annotation { "Feature Type Name" : "Feature", "Feature Type Description" : "" }
export const myFeature = defineFeature(function(context is Context, id is Id, definition is map)
    precondition{}
    {
        {
            var Q0;
            Q0=qCreatedBy(makeId("Top.planeOp"),FACE);
            var sketch = newSketch(context, id + "F0", { "sketchPlane" : qUnion([Q0])});
            skLineSegment(sketch, "E0.bottom", {"start": v(75, -105) * mm, "end": v(-75, -105) * mm});
            skLineSegment(sketch, "E0.top", {"start": v(75, 105) * mm, "end": v(-75, 105) * mm});
            skLineSegment(sketch, "E0.left", {"start": v(75, -105) * mm, "end": v(75, 105) * mm});
            skLineSegment(sketch, "E0.right", {"start": v(-75, -105) * mm, "end": v(-75, 105) * mm});
            skPoint(sketch, "E0.middle", {"position": v(0, 0) * mm});
            skLineSegment(sketch, "E1.bottom", {"start": v(77, -107) * mm, "end": v(-77, -107) * mm});
            skLineSegment(sketch, "E1.top", {"start": v(77, 107) * mm, "end": v(-77, 107) * mm});
            skLineSegment(sketch, "E1.left", {"start": v(77, -107) * mm, "end": v(77, 107) * mm});
            skLineSegment(sketch, "E1.right", {"start": v(-77, -107) * mm, "end": v(-77, 107) * mm});
            skSolve(sketch);
        }
        {
            var Q0;
            Q0=makeQuery(id+"F0.imprint","IMPRINT",FACE,{"disambiguationData":[TD([[makeQuery(id+"F0.imprint","IMPRINT",EDGE,{"derivedFrom":sQuery(id+"F0.wireOp",EDGE,"E0.bottom")}),-1.0]])]});
            extrude(context, id + "F1", {"entities" : qUnion([Q0]), "depth" : 8 * mm, "offsetDistance" : 25 * mm});
        }
        {
            var Q0;
            Q0=makeQuery(id+"F0.imprint","IMPRINT",FACE,{"disambiguationData":[TD([[makeQuery(id+"F0.imprint","IMPRINT",EDGE,{"derivedFrom":sQuery(id+"F0.wireOp",EDGE,"E0.bottom")}),1.0]])]});
            extrude(context, id + "F2", {"entities" : qUnion([Q0]), "operationType" : NewBodyOperationType.ADD, "depth" : 100 * mm, "offsetDistance" : 25 * mm});
        }
        {
            var Q0;
            Q0=makeQuery(id+"F2.opExtrude","SWEPT_FACE",FACE,{"disambiguationData":[OSD([sQuery(id+"F0.wireOp",EDGE,"E0.right")])]});
            var sketch = newSketch(context, id + "F3", { "sketchPlane" : qUnion([Q0])});
            skLineSegment(sketch, "E2.bottom", {"start": v(-6.25, 88.1) * mm, "end": v(14.25, 88.1) * mm});
            skLineSegment(sketch, "E2.top", {"start": v(-6.25, 76.6) * mm, "end": v(14.25, 76.6) * mm});
            skLineSegment(sketch, "E2.left", {"start": v(-6.25, 88.1) * mm, "end": v(-6.25, 76.6) * mm});
            skLineSegment(sketch, "E2.right", {"start": v(14.25, 88.1) * mm, "end": v(14.25, 76.6) * mm});
            skLineSegment(sketch, "E3.bottom", {"start": v(-7, 38.82) * mm, "end": v(15, 38.82) * mm});
            skLineSegment(sketch, "E3.top", {"start": v(-7, 15.82) * mm, "end": v(15, 15.82) * mm});
            skLineSegment(sketch, "E3.left", {"start": v(-7, 38.82) * mm, "end": v(-7, 15.82) * mm});
            skLineSegment(sketch, "E3.right", {"start": v(15, 38.82) * mm, "end": v(15, 15.82) * mm});
            skLineSegment(sketch, "E4.bottom", {"start": v(39.95, 34) * mm, "end": v(59.95, 34) * mm});
            skLineSegment(sketch, "E4.top", {"start": v(39.95, 26) * mm, "end": v(59.95, 26) * mm});
            skLineSegment(sketch, "E4.left", {"start": v(59.95, 34) * mm, "end": v(59.95, 26) * mm});
            skLineSegment(sketch, "E4.right", {"start": v(39.95, 34) * mm, "end": v(39.95, 26) * mm});
            skPoint(sketch, "E5", {"position": v(49.95, 34) * mm});
            skLineSegment(sketch, "E6.0.1.0", {"start": v(59.95, 61) * mm, "end": v(59.95, 53) * mm});
            skLineSegment(sketch, "E6.0.1.1", {"start": v(39.95, 53) * mm, "end": v(59.95, 53) * mm});
            skLineSegment(sketch, "E6.0.1.2", {"start": v(39.95, 61) * mm, "end": v(39.95, 53) * mm});
            skLineSegment(sketch, "E6.0.1.3", {"start": v(39.95, 61) * mm, "end": v(59.95, 61) * mm});
            skPoint(sketch, "E6.0.1.4", {"position": v(49.95, 61) * mm});
            skLineSegment(sketch, "E6.0.2.0", {"start": v(59.95, 88) * mm, "end": v(59.95, 80) * mm});
            skLineSegment(sketch, "E6.0.2.1", {"start": v(39.95, 80) * mm, "end": v(59.95, 80) * mm});
            skLineSegment(sketch, "E6.0.2.2", {"start": v(39.95, 88) * mm, "end": v(39.95, 80) * mm});
            skLineSegment(sketch, "E6.0.2.3", {"start": v(39.95, 88) * mm, "end": v(59.95, 88) * mm});
            skPoint(sketch, "E6.0.2.4", {"position": v(49.95, 88) * mm});
            skLineSegment(sketch, "E6.direction1", {"start": v(39.95, 26) * mm, "end": v(62.2, 26) * mm, "construction": true});
            skLineSegment(sketch, "E6.direction2", {"start": v(39.95, 26) * mm, "end": v(39.95, 53) * mm, "construction": true});
            skLineSegment(sketch, "E7.bottom", {"start": v(-6.25, 63.2) * mm, "end": v(14.25, 63.2) * mm});
            skLineSegment(sketch, "E7.top", {"start": v(-6.25, 53.7) * mm, "end": v(14.25, 53.7) * mm});
            skLineSegment(sketch, "E7.left", {"start": v(-6.25, 63.2) * mm, "end": v(-6.25, 53.7) * mm});
            skLineSegment(sketch, "E7.right", {"start": v(14.25, 63.2) * mm, "end": v(14.25, 53.7) * mm});
            skCircle(sketch, "E8", {"center": v(-55, 68) * mm, "radius": 4.5 * mm});
            skPoint(sketch, "E9", {"position": v(-79.5, 38) * mm});
            skPoint(sketch, "E10", {"position": v(77.48, 100) * mm});
            skPoint(sketch, "E11", {"position": v(77.48, 0) * mm});
            skPoint(sketch, "E12", {"position": v(105, 100) * mm});
            skPoint(sketch, "E13", {"position": v(-105, 100) * mm});
            skCircle(sketch, "E14", {"center": v(-79.5, 38) * mm, "radius": 3.5 * mm});
            skPoint(sketch, "E15", {"position": v(4, 15.82) * mm});
            skPoint(sketch, "E16", {"position": v(4, 63.2) * mm});
            skPoint(sketch, "E17", {"position": v(4, 76.6) * mm});
            skSolve(sketch);
        }
        {
            var Q0;
            Q0=makeQuery(id+"F3.imprint","IMPRINT",FACE,{"disambiguationData":[TD([[makeQuery(id+"F3.imprint","IMPRINT",EDGE,{"derivedFrom":sQuery(id+"F3.wireOp",EDGE,"E2.bottom")}),-1.0]])]});
            var Q1;
            Q1=makeQuery(id+"F3.imprint","IMPRINT",FACE,{"disambiguationData":[TD([[makeQuery(id+"F3.imprint","IMPRINT",EDGE,{"derivedFrom":sQuery(id+"F3.wireOp",EDGE,"E3.bottom")}),-1.0]])]});
            var Q2;
            Q2=makeQuery(id+"F3.imprint","IMPRINT",FACE,{"disambiguationData":[TD([[makeQuery(id+"F3.imprint","IMPRINT",EDGE,{"derivedFrom":sQuery(id+"F3.wireOp",EDGE,"E4.bottom")}),-1.0]])]});
            var Q3;
            Q3=makeQuery(id+"F3.imprint","IMPRINT",FACE,{"disambiguationData":[TD([[makeQuery(id+"F3.imprint","IMPRINT",EDGE,{"derivedFrom":sQuery(id+"F3.wireOp",EDGE,"E6.0.1.0")}),-1.0]])]});
            var Q4;
            Q4=makeQuery(id+"F3.imprint","IMPRINT",FACE,{"disambiguationData":[TD([[makeQuery(id+"F3.imprint","IMPRINT",EDGE,{"derivedFrom":sQuery(id+"F3.wireOp",EDGE,"E6.0.2.0")}),-1.0]])]});
            var Q5;
            Q5=makeQuery(id+"F3.imprint","IMPRINT",FACE,{"disambiguationData":[TD([[makeQuery(id+"F3.imprint","IMPRINT",EDGE,{"derivedFrom":sQuery(id+"F3.wireOp",EDGE,"E7.bottom")}),-1.0]])]});
            var Q6;
            Q6=makeQuery(id+"F3.imprint","IMPRINT",FACE,{"disambiguationData":[TD([[makeQuery(id+"F3.imprint","IMPRINT",EDGE,{"derivedFrom":sQuery(id+"F3.wireOp",EDGE,"E8")}),1.0]])]});
            extrude(context, id + "F4", {"entities" : qUnion([Q0, Q1, Q2, Q3, Q4, Q5, Q6]), "operationType" : NewBodyOperationType.REMOVE, "endBound" : BoundingType.UP_TO_NEXT, "oppositeDirection" : true, "depth" : 25 * mm, "offsetDistance" : 25 * mm});
        }
        {
            var Q0;
            Q0=makeQuery(id+"F2.opExtrude","SWEPT_FACE",FACE,{"disambiguationData":[OSD([sQuery(id+"F0.wireOp",EDGE,"E1.right")])]});
            var sketch = newSketch(context, id + "F5", { "sketchPlane" : qUnion([Q0])});
            skPoint(sketch, "E18", {"position": v(-16, 82.35) * mm});
            skPoint(sketch, "E18.positionSnap0", {"position": v(-14.25, 82.35) * mm});
            skPoint(sketch, "E19.positionSnap0", {"position": v(6.25, 82.35) * mm});
            skPoint(sketch, "E20", {"position": v(9.75, 27.32) * mm});
            skPoint(sketch, "E20.positionSnap0", {"position": v(7, 27.32) * mm});
            skPoint(sketch, "E21", {"position": v(-17.75, 27.32) * mm});
            skPoint(sketch, "E21.positionSnap0", {"position": v(-15, 27.32) * mm});
            skPoint(sketch, "E22", {"position": v(55, 68) * mm});
            skPoint(sketch, "E23", {"position": v(62.5, 68) * mm});
            skPoint(sketch, "E24", {"position": v(47.5, 68) * mm});
            skPoint(sketch, "E25", {"position": v(8, 82.35) * mm});
            skPoint(sketch, "E26", {"position": v(9.75, 58.44) * mm});
            skPoint(sketch, "E26.positionSnap0", {"position": v(6.25, 58.44) * mm});
            skPoint(sketch, "E27", {"position": v(-17.75, 58.44) * mm});
            skPoint(sketch, "E27.positionSnap0", {"position": v(-14.25, 58.44) * mm});
            skSolve(sketch);
        }
        {
            var Q0;
            Q0=sQuery(id+"F5.wireOp",VERTEX,"E18");
            var Q1;
            Q1=sQuery(id+"F5.wireOp",VERTEX,"E19");
            var Q2;
            Q2=sQuery(id+"F5.wireOp",VERTEX,"E25");
            var Q3;
            Q3=sQuery(id+"F5.wireOp",VERTEX,"E27");
            var Q4;
            Q4=sQuery(id+"F5.wireOp",VERTEX,"E26");
            var Q5;
            Q5=makeQuery(id+"F1.opExtrude","SWEPT_BODY",BODY,{"disambiguationData":[OSD([sQuery(id+"F0.wireOp",EDGE,"E0.bottom"),sQuery(id+"F0.wireOp",EDGE,"E0.top"),sQuery(id+"F0.wireOp",EDGE,"E0.left"),sQuery(id+"F0.wireOp",EDGE,"E0.right")])]});
            hole(context, id + "F6", {"style" : HoleStyle.SIMPLE, "endStyle" : HoleEndStyle.BLIND, "holeDiameter" : 2.2 * mm, "majorDiameter" : 5 * mm, "holeDepth" : 5 * mm, "isTappedThrough" : true, "tappedDepth" : 12 * mm, "tapClearance" : 3, "locations" : qUnion([Q0, Q1, Q2, Q3, Q4]), "scope" : qUnion([Q5])});
        }
        {
            var Q0;
            Q0=sQuery(id+"F5.wireOp",VERTEX,"E20");
            var Q1;
            Q1=sQuery(id+"F5.wireOp",VERTEX,"E21");
            var Q2;
            Q2=makeQuery(id+"F1.opExtrude","SWEPT_BODY",BODY,{"disambiguationData":[OSD([sQuery(id+"F0.wireOp",EDGE,"E0.bottom"),sQuery(id+"F0.wireOp",EDGE,"E0.top"),sQuery(id+"F0.wireOp",EDGE,"E0.left"),sQuery(id+"F0.wireOp",EDGE,"E0.right")])]});
            hole(context, id + "F7", {"style" : HoleStyle.SIMPLE, "endStyle" : HoleEndStyle.BLIND, "holeDiameter" : 3.3 * mm, "majorDiameter" : 5 * mm, "holeDepth" : 5 * mm, "isTappedThrough" : true, "tappedDepth" : 12 * mm, "tapClearance" : 3, "locations" : qUnion([Q0, Q1]), "scope" : qUnion([Q2])});
        }
        {
            var Q0;
            Q0=makeQuery(id+"F2.opExtrude","SWEPT_FACE",FACE,{"disambiguationData":[OSD([sQuery(id+"F0.wireOp",EDGE,"E1.right")])]});
            var sketch = newSketch(context, id + "F8", { "sketchPlane" : qUnion([Q0])});
            skText(sketch, "E28", { "text": "RADAR INPUT", "fontName": "OpenSans-Regular.ttf"});
            skText(sketch, "E29", { "text": "FRONT CAMERA INPUT", "fontName": "OpenSans-Regular.ttf"});
            skText(sketch, "E30", { "text": "MONITOR OUT", "fontName": "OpenSans-Regular.ttf"});
            skText(sketch, "E31", { "text": "REAR CAMERA INPUT", "fontName": "OpenSans-Regular.ttf"});
            skText(sketch, "E32", { "text": "ETHERNET", "fontName": "OpenSans-Regular.ttf"});
            skText(sketch, "E33", { "text": "POWER", "fontName": "OpenSans-Regular.ttf"});
            skText(sketch, "E34", { "text": "SIDE CAMERA INPUT", "fontName": "OpenSans-Regular.ttf"});
            skText(sketch, "E35", { "text": "GPS", "fontName": "OpenSans-Regular.ttf"});
            const initialGuessF8  = {"E28": [-0.01525, 0.06005, 1, 0, 0.00195], "E29": [-0.05995, 0.07665, 1, 0, 0.00135], "E30": [-0.01525, 0.03621, 1, 0, 0.00179], "E31": [-0.05995, 0.02254, 1, 0, 0.00146], "E32": [0.0215, 0.03581, 1, 0, 0.00219], "E33": [0.055, 0.04946, 1, 0, 0.00204], "E34": [-0.05995, 0.0495, 1, 0, 0.0015], "E35": [0.07792, 0.0306, 1, 0, 0.0019]};
            skSetInitialGuess(sketch, initialGuessF8);
            skSolve(sketch);
        }
        {
            var Q0;
            Q0=makeQuery(id+"F8.imprint","IMPRINT",FACE,{"disambiguationData":[TD([[makeQuery(id+"F8.imprint","IMPRINT",EDGE,{"derivedFrom":sQuery(id+"F8.wireOp",EDGE,"E29.sketch_text.stroke-0")}),-1.0]])]});
            var Q1;
            Q1=makeQuery(id+"F8.imprint","IMPRINT",FACE,{"disambiguationData":[TD([[makeQuery(id+"F8.imprint","IMPRINT",EDGE,{"derivedFrom":sQuery(id+"F8.wireOp",EDGE,"E29.sketch_text.stroke-10")}),-1.0]])]});
            var Q2;
            Q2=makeQuery(id+"F8.imprint","IMPRINT",FACE,{"disambiguationData":[TD([[makeQuery(id+"F8.imprint","IMPRINT",EDGE,{"derivedFrom":sQuery(id+"F8.wireOp",EDGE,"E29.sketch_text.stroke-28")}),-1.0]])]});
            var Q3;
            Q3=makeQuery(id+"F8.imprint","IMPRINT",FACE,{"disambiguationData":[TD([[makeQuery(id+"F8.imprint","IMPRINT",EDGE,{"derivedFrom":sQuery(id+"F8.wireOp",EDGE,"E29.sketch_text.stroke-44")}),-1.0]])]});
            var Q4;
            Q4=makeQuery(id+"F8.imprint","IMPRINT",FACE,{"disambiguationData":[TD([[makeQuery(id+"F8.imprint","IMPRINT",EDGE,{"derivedFrom":sQuery(id+"F8.wireOp",EDGE,"E29.sketch_text.stroke-59")}),-1.0]])]});
            var Q5;
            Q5=makeQuery(id+"F8.imprint","IMPRINT",FACE,{"disambiguationData":[TD([[makeQuery(id+"F8.imprint","IMPRINT",EDGE,{"derivedFrom":sQuery(id+"F8.wireOp",EDGE,"E29.sketch_text.stroke-67")}),-1.0]])]});
            var Q6;
            Q6=makeQuery(id+"F8.imprint","IMPRINT",FACE,{"disambiguationData":[TD([[makeQuery(id+"F8.imprint","IMPRINT",EDGE,{"derivedFrom":sQuery(id+"F8.wireOp",EDGE,"E29.sketch_text.stroke-82")}),-1.0]])]});
            var Q7;
            Q7=makeQuery(id+"F8.imprint","IMPRINT",FACE,{"disambiguationData":[TD([[makeQuery(id+"F8.imprint","IMPRINT",EDGE,{"derivedFrom":sQuery(id+"F8.wireOp",EDGE,"E29.sketch_text.stroke-95")}),-1.0]])]});
            var Q8;
            Q8=makeQuery(id+"F8.imprint","IMPRINT",FACE,{"disambiguationData":[TD([[makeQuery(id+"F8.imprint","IMPRINT",EDGE,{"derivedFrom":sQuery(id+"F8.wireOp",EDGE,"E29.sketch_text.stroke-113")}),-1.0]])]});
            var Q9;
            Q9=makeQuery(id+"F8.imprint","IMPRINT",FACE,{"disambiguationData":[TD([[makeQuery(id+"F8.imprint","IMPRINT",EDGE,{"derivedFrom":sQuery(id+"F8.wireOp",EDGE,"E29.sketch_text.stroke-125")}),-1.0]])]});
            var Q10;
            Q10=makeQuery(id+"F8.imprint","IMPRINT",FACE,{"disambiguationData":[TD([[makeQuery(id+"F8.imprint","IMPRINT",EDGE,{"derivedFrom":sQuery(id+"F8.wireOp",EDGE,"E29.sketch_text.stroke-143")}),-1.0]])]});
            var Q11;
            Q11=makeQuery(id+"F8.imprint","IMPRINT",FACE,{"disambiguationData":[TD([[makeQuery(id+"F8.imprint","IMPRINT",EDGE,{"derivedFrom":sQuery(id+"F8.wireOp",EDGE,"E29.sketch_text.stroke-156")}),-1.0]])]});
            var Q12;
            Q12=makeQuery(id+"F8.imprint","IMPRINT",FACE,{"disambiguationData":[TD([[makeQuery(id+"F8.imprint","IMPRINT",EDGE,{"derivedFrom":sQuery(id+"F8.wireOp",EDGE,"E29.sketch_text.stroke-160")}),-1.0]])]});
            var Q13;
            Q13=makeQuery(id+"F8.imprint","IMPRINT",FACE,{"disambiguationData":[TD([[makeQuery(id+"F8.imprint","IMPRINT",EDGE,{"derivedFrom":sQuery(id+"F8.wireOp",EDGE,"E29.sketch_text.stroke-175")}),-1.0]])]});
            var Q14;
            Q14=makeQuery(id+"F8.imprint","IMPRINT",FACE,{"disambiguationData":[TD([[makeQuery(id+"F8.imprint","IMPRINT",EDGE,{"derivedFrom":sQuery(id+"F8.wireOp",EDGE,"E29.sketch_text.stroke-190")}),-1.0]])]});
            var Q15;
            Q15=makeQuery(id+"F8.imprint","IMPRINT",FACE,{"disambiguationData":[TD([[makeQuery(id+"F8.imprint","IMPRINT",EDGE,{"derivedFrom":sQuery(id+"F8.wireOp",EDGE,"E29.sketch_text.stroke-204")}),-1.0]])]});
            var Q16;
            Q16=makeQuery(id+"F8.imprint","IMPRINT",FACE,{"disambiguationData":[TD([[makeQuery(id+"F8.imprint","IMPRINT",EDGE,{"derivedFrom":sQuery(id+"F8.wireOp",EDGE,"ac93d7fe-7f5a-423e-b7ee-c134c41d6a74.sketch_text.stroke-0")}),-1.0]])]});
            var Q17;
            Q17=makeQuery(id+"F8.imprint","IMPRINT",FACE,{"disambiguationData":[TD([[makeQuery(id+"F8.imprint","IMPRINT",EDGE,{"derivedFrom":sQuery(id+"F8.wireOp",EDGE,"ac93d7fe-7f5a-423e-b7ee-c134c41d6a74.sketch_text.stroke-25")}),-1.0]])]});
            var Q18;
            Q18=makeQuery(id+"F8.imprint","IMPRINT",FACE,{"disambiguationData":[TD([[makeQuery(id+"F8.imprint","IMPRINT",EDGE,{"derivedFrom":sQuery(id+"F8.wireOp",EDGE,"ac93d7fe-7f5a-423e-b7ee-c134c41d6a74.sketch_text.stroke-29")}),-1.0]])]});
            var Q19;
            Q19=makeQuery(id+"F8.imprint","IMPRINT",FACE,{"disambiguationData":[TD([[makeQuery(id+"F8.imprint","IMPRINT",EDGE,{"derivedFrom":sQuery(id+"F8.wireOp",EDGE,"ac93d7fe-7f5a-423e-b7ee-c134c41d6a74.sketch_text.stroke-43")}),-1.0]])]});
            var Q20;
            Q20=makeQuery(id+"F8.imprint","IMPRINT",FACE,{"disambiguationData":[TD([[makeQuery(id+"F8.imprint","IMPRINT",EDGE,{"derivedFrom":sQuery(id+"F8.wireOp",EDGE,"ac93d7fe-7f5a-423e-b7ee-c134c41d6a74.sketch_text.stroke-55")}),-1.0]])]});
            var Q21;
            Q21=makeQuery(id+"F8.imprint","IMPRINT",FACE,{"disambiguationData":[TD([[makeQuery(id+"F8.imprint","IMPRINT",EDGE,{"derivedFrom":sQuery(id+"F8.wireOp",EDGE,"ac93d7fe-7f5a-423e-b7ee-c134c41d6a74.sketch_text.stroke-70")}),-1.0]])]});
            var Q22;
            Q22=makeQuery(id+"F8.imprint","IMPRINT",FACE,{"disambiguationData":[TD([[makeQuery(id+"F8.imprint","IMPRINT",EDGE,{"derivedFrom":sQuery(id+"F8.wireOp",EDGE,"ac93d7fe-7f5a-423e-b7ee-c134c41d6a74.sketch_text.stroke-83")}),-1.0]])]});
            var Q23;
            Q23=makeQuery(id+"F8.imprint","IMPRINT",FACE,{"disambiguationData":[TD([[makeQuery(id+"F8.imprint","IMPRINT",EDGE,{"derivedFrom":sQuery(id+"F8.wireOp",EDGE,"ac93d7fe-7f5a-423e-b7ee-c134c41d6a74.sketch_text.stroke-101")}),-1.0]])]});
            var Q24;
            Q24=makeQuery(id+"F8.imprint","IMPRINT",FACE,{"disambiguationData":[TD([[makeQuery(id+"F8.imprint","IMPRINT",EDGE,{"derivedFrom":sQuery(id+"F8.wireOp",EDGE,"ac93d7fe-7f5a-423e-b7ee-c134c41d6a74.sketch_text.stroke-113")}),-1.0]])]});
            var Q25;
            Q25=makeQuery(id+"F8.imprint","IMPRINT",FACE,{"disambiguationData":[TD([[makeQuery(id+"F8.imprint","IMPRINT",EDGE,{"derivedFrom":sQuery(id+"F8.wireOp",EDGE,"ac93d7fe-7f5a-423e-b7ee-c134c41d6a74.sketch_text.stroke-131")}),-1.0]])]});
            var Q26;
            Q26=makeQuery(id+"F8.imprint","IMPRINT",FACE,{"disambiguationData":[TD([[makeQuery(id+"F8.imprint","IMPRINT",EDGE,{"derivedFrom":sQuery(id+"F8.wireOp",EDGE,"ac93d7fe-7f5a-423e-b7ee-c134c41d6a74.sketch_text.stroke-144")}),-1.0]])]});
            var Q27;
            Q27=makeQuery(id+"F8.imprint","IMPRINT",FACE,{"disambiguationData":[TD([[makeQuery(id+"F8.imprint","IMPRINT",EDGE,{"derivedFrom":sQuery(id+"F8.wireOp",EDGE,"ac93d7fe-7f5a-423e-b7ee-c134c41d6a74.sketch_text.stroke-148")}),-1.0]])]});
            var Q28;
            Q28=makeQuery(id+"F8.imprint","IMPRINT",FACE,{"disambiguationData":[TD([[makeQuery(id+"F8.imprint","IMPRINT",EDGE,{"derivedFrom":sQuery(id+"F8.wireOp",EDGE,"ac93d7fe-7f5a-423e-b7ee-c134c41d6a74.sketch_text.stroke-163")}),-1.0]])]});
            var Q29;
            Q29=makeQuery(id+"F8.imprint","IMPRINT",FACE,{"disambiguationData":[TD([[makeQuery(id+"F8.imprint","IMPRINT",EDGE,{"derivedFrom":sQuery(id+"F8.wireOp",EDGE,"ac93d7fe-7f5a-423e-b7ee-c134c41d6a74.sketch_text.stroke-178")}),-1.0]])]});
            var Q30;
            Q30=makeQuery(id+"F8.imprint","IMPRINT",FACE,{"disambiguationData":[TD([[makeQuery(id+"F8.imprint","IMPRINT",EDGE,{"derivedFrom":sQuery(id+"F8.wireOp",EDGE,"ac93d7fe-7f5a-423e-b7ee-c134c41d6a74.sketch_text.stroke-192")}),-1.0]])]});
            var Q31;
            Q31=makeQuery(id+"F8.imprint","IMPRINT",FACE,{"disambiguationData":[TD([[makeQuery(id+"F8.imprint","IMPRINT",EDGE,{"derivedFrom":sQuery(id+"F8.wireOp",EDGE,"E31.sketch_text.stroke-0")}),-1.0]])]});
            var Q32;
            Q32=makeQuery(id+"F8.imprint","IMPRINT",FACE,{"disambiguationData":[TD([[makeQuery(id+"F8.imprint","IMPRINT",EDGE,{"derivedFrom":sQuery(id+"F8.wireOp",EDGE,"E31.sketch_text.stroke-18")}),-1.0]])]});
            var Q33;
            Q33=makeQuery(id+"F8.imprint","IMPRINT",FACE,{"disambiguationData":[TD([[makeQuery(id+"F8.imprint","IMPRINT",EDGE,{"derivedFrom":sQuery(id+"F8.wireOp",EDGE,"E31.sketch_text.stroke-30")}),-1.0]])]});
            var Q34;
            Q34=makeQuery(id+"F8.imprint","IMPRINT",FACE,{"disambiguationData":[TD([[makeQuery(id+"F8.imprint","IMPRINT",EDGE,{"derivedFrom":sQuery(id+"F8.wireOp",EDGE,"E31.sketch_text.stroke-43")}),-1.0]])]});
            var Q35;
            Q35=makeQuery(id+"F8.imprint","IMPRINT",FACE,{"disambiguationData":[TD([[makeQuery(id+"F8.imprint","IMPRINT",EDGE,{"derivedFrom":sQuery(id+"F8.wireOp",EDGE,"E31.sketch_text.stroke-61")}),-1.0]])]});
            var Q36;
            Q36=makeQuery(id+"F8.imprint","IMPRINT",FACE,{"disambiguationData":[TD([[makeQuery(id+"F8.imprint","IMPRINT",EDGE,{"derivedFrom":sQuery(id+"F8.wireOp",EDGE,"E31.sketch_text.stroke-76")}),-1.0]])]});
            var Q37;
            Q37=makeQuery(id+"F8.imprint","IMPRINT",FACE,{"disambiguationData":[TD([[makeQuery(id+"F8.imprint","IMPRINT",EDGE,{"derivedFrom":sQuery(id+"F8.wireOp",EDGE,"E31.sketch_text.stroke-89")}),-1.0]])]});
            var Q38;
            Q38=makeQuery(id+"F8.imprint","IMPRINT",FACE,{"disambiguationData":[TD([[makeQuery(id+"F8.imprint","IMPRINT",EDGE,{"derivedFrom":sQuery(id+"F8.wireOp",EDGE,"E31.sketch_text.stroke-107")}),-1.0]])]});
            var Q39;
            Q39=makeQuery(id+"F8.imprint","IMPRINT",FACE,{"disambiguationData":[TD([[makeQuery(id+"F8.imprint","IMPRINT",EDGE,{"derivedFrom":sQuery(id+"F8.wireOp",EDGE,"E31.sketch_text.stroke-119")}),-1.0]])]});
            var Q40;
            Q40=makeQuery(id+"F8.imprint","IMPRINT",FACE,{"disambiguationData":[TD([[makeQuery(id+"F8.imprint","IMPRINT",EDGE,{"derivedFrom":sQuery(id+"F8.wireOp",EDGE,"E31.sketch_text.stroke-137")}),-1.0]])]});
            var Q41;
            Q41=makeQuery(id+"F8.imprint","IMPRINT",FACE,{"disambiguationData":[TD([[makeQuery(id+"F8.imprint","IMPRINT",EDGE,{"derivedFrom":sQuery(id+"F8.wireOp",EDGE,"E31.sketch_text.stroke-150")}),-1.0]])]});
            var Q42;
            Q42=makeQuery(id+"F8.imprint","IMPRINT",FACE,{"disambiguationData":[TD([[makeQuery(id+"F8.imprint","IMPRINT",EDGE,{"derivedFrom":sQuery(id+"F8.wireOp",EDGE,"E31.sketch_text.stroke-154")}),-1.0]])]});
            var Q43;
            Q43=makeQuery(id+"F8.imprint","IMPRINT",FACE,{"disambiguationData":[TD([[makeQuery(id+"F8.imprint","IMPRINT",EDGE,{"derivedFrom":sQuery(id+"F8.wireOp",EDGE,"E31.sketch_text.stroke-169")}),-1.0]])]});
            var Q44;
            Q44=makeQuery(id+"F8.imprint","IMPRINT",FACE,{"disambiguationData":[TD([[makeQuery(id+"F8.imprint","IMPRINT",EDGE,{"derivedFrom":sQuery(id+"F8.wireOp",EDGE,"E31.sketch_text.stroke-184")}),-1.0]])]});
            var Q45;
            Q45=makeQuery(id+"F8.imprint","IMPRINT",FACE,{"disambiguationData":[TD([[makeQuery(id+"F8.imprint","IMPRINT",EDGE,{"derivedFrom":sQuery(id+"F8.wireOp",EDGE,"E31.sketch_text.stroke-198")}),-1.0]])]});
            var Q46;
            Q46=makeQuery(id+"F8.imprint","IMPRINT",FACE,{"disambiguationData":[TD([[makeQuery(id+"F8.imprint","IMPRINT",EDGE,{"derivedFrom":sQuery(id+"F8.wireOp",EDGE,"E32.sketch_text.stroke-0")}),-1.0]])]});
            var Q47;
            Q47=makeQuery(id+"F8.imprint","IMPRINT",FACE,{"disambiguationData":[TD([[makeQuery(id+"F8.imprint","IMPRINT",EDGE,{"derivedFrom":sQuery(id+"F8.wireOp",EDGE,"E32.sketch_text.stroke-12")}),-1.0]])]});
            var Q48;
            Q48=makeQuery(id+"F8.imprint","IMPRINT",FACE,{"disambiguationData":[TD([[makeQuery(id+"F8.imprint","IMPRINT",EDGE,{"derivedFrom":sQuery(id+"F8.wireOp",EDGE,"E32.sketch_text.stroke-20")}),-1.0]])]});
            var Q49;
            Q49=makeQuery(id+"F8.imprint","IMPRINT",FACE,{"disambiguationData":[TD([[makeQuery(id+"F8.imprint","IMPRINT",EDGE,{"derivedFrom":sQuery(id+"F8.wireOp",EDGE,"E32.sketch_text.stroke-32")}),-1.0]])]});
            var Q50;
            Q50=makeQuery(id+"F8.imprint","IMPRINT",FACE,{"disambiguationData":[TD([[makeQuery(id+"F8.imprint","IMPRINT",EDGE,{"derivedFrom":sQuery(id+"F8.wireOp",EDGE,"E32.sketch_text.stroke-44")}),-1.0]])]});
            var Q51;
            Q51=makeQuery(id+"F8.imprint","IMPRINT",FACE,{"disambiguationData":[TD([[makeQuery(id+"F8.imprint","IMPRINT",EDGE,{"derivedFrom":sQuery(id+"F8.wireOp",EDGE,"E32.sketch_text.stroke-62")}),-1.0]])]});
            var Q52;
            Q52=makeQuery(id+"F8.imprint","IMPRINT",FACE,{"disambiguationData":[TD([[makeQuery(id+"F8.imprint","IMPRINT",EDGE,{"derivedFrom":sQuery(id+"F8.wireOp",EDGE,"E32.sketch_text.stroke-77")}),-1.0]])]});
            var Q53;
            Q53=makeQuery(id+"F8.imprint","IMPRINT",FACE,{"disambiguationData":[TD([[makeQuery(id+"F8.imprint","IMPRINT",EDGE,{"derivedFrom":sQuery(id+"F8.wireOp",EDGE,"E32.sketch_text.stroke-89")}),-1.0]])]});
            var Q54;
            Q54=makeQuery(id+"F8.imprint","IMPRINT",FACE,{"disambiguationData":[TD([[makeQuery(id+"F8.imprint","IMPRINT",EDGE,{"derivedFrom":sQuery(id+"F8.wireOp",EDGE,"E30.sketch_text.stroke-0")}),-1.0]])]});
            var Q55;
            Q55=makeQuery(id+"F8.imprint","IMPRINT",FACE,{"disambiguationData":[TD([[makeQuery(id+"F8.imprint","IMPRINT",EDGE,{"derivedFrom":sQuery(id+"F8.wireOp",EDGE,"E30.sketch_text.stroke-18")}),-1.0]])]});
            var Q56;
            Q56=makeQuery(id+"F8.imprint","IMPRINT",FACE,{"disambiguationData":[TD([[makeQuery(id+"F8.imprint","IMPRINT",EDGE,{"derivedFrom":sQuery(id+"F8.wireOp",EDGE,"E30.sketch_text.stroke-34")}),-1.0]])]});
            var Q57;
            Q57=makeQuery(id+"F8.imprint","IMPRINT",FACE,{"disambiguationData":[TD([[makeQuery(id+"F8.imprint","IMPRINT",EDGE,{"derivedFrom":sQuery(id+"F8.wireOp",EDGE,"E30.sketch_text.stroke-49")}),-1.0]])]});
            var Q58;
            Q58=makeQuery(id+"F8.imprint","IMPRINT",FACE,{"disambiguationData":[TD([[makeQuery(id+"F8.imprint","IMPRINT",EDGE,{"derivedFrom":sQuery(id+"F8.wireOp",EDGE,"E30.sketch_text.stroke-53")}),-1.0]])]});
            var Q59;
            Q59=makeQuery(id+"F8.imprint","IMPRINT",FACE,{"disambiguationData":[TD([[makeQuery(id+"F8.imprint","IMPRINT",EDGE,{"derivedFrom":sQuery(id+"F8.wireOp",EDGE,"E30.sketch_text.stroke-61")}),-1.0]])]});
            var Q60;
            Q60=makeQuery(id+"F8.imprint","IMPRINT",FACE,{"disambiguationData":[TD([[makeQuery(id+"F8.imprint","IMPRINT",EDGE,{"derivedFrom":sQuery(id+"F8.wireOp",EDGE,"E30.sketch_text.stroke-77")}),-1.0]])]});
            var Q61;
            Q61=makeQuery(id+"F8.imprint","IMPRINT",FACE,{"disambiguationData":[TD([[makeQuery(id+"F8.imprint","IMPRINT",EDGE,{"derivedFrom":sQuery(id+"F8.wireOp",EDGE,"E30.sketch_text.stroke-95")}),-1.0]])]});
            var Q62;
            Q62=makeQuery(id+"F8.imprint","IMPRINT",FACE,{"disambiguationData":[TD([[makeQuery(id+"F8.imprint","IMPRINT",EDGE,{"derivedFrom":sQuery(id+"F8.wireOp",EDGE,"E30.sketch_text.stroke-111")}),-1.0]])]});
            var Q63;
            Q63=makeQuery(id+"F8.imprint","IMPRINT",FACE,{"disambiguationData":[TD([[makeQuery(id+"F8.imprint","IMPRINT",EDGE,{"derivedFrom":sQuery(id+"F8.wireOp",EDGE,"E30.sketch_text.stroke-125")}),-1.0]])]});
            var Q64;
            Q64=makeQuery(id+"F8.imprint","IMPRINT",FACE,{"disambiguationData":[TD([[makeQuery(id+"F8.imprint","IMPRINT",EDGE,{"derivedFrom":sQuery(id+"F8.wireOp",EDGE,"E28.sketch_text.stroke-0")}),-1.0]])]});
            var Q65;
            Q65=makeQuery(id+"F8.imprint","IMPRINT",FACE,{"disambiguationData":[TD([[makeQuery(id+"F8.imprint","IMPRINT",EDGE,{"derivedFrom":sQuery(id+"F8.wireOp",EDGE,"E28.sketch_text.stroke-18")}),-1.0]])]});
            var Q66;
            Q66=makeQuery(id+"F8.imprint","IMPRINT",FACE,{"disambiguationData":[TD([[makeQuery(id+"F8.imprint","IMPRINT",EDGE,{"derivedFrom":sQuery(id+"F8.wireOp",EDGE,"E28.sketch_text.stroke-31")}),-1.0]])]});
            var Q67;
            Q67=makeQuery(id+"F8.imprint","IMPRINT",FACE,{"disambiguationData":[TD([[makeQuery(id+"F8.imprint","IMPRINT",EDGE,{"derivedFrom":sQuery(id+"F8.wireOp",EDGE,"E28.sketch_text.stroke-45")}),-1.0]])]});
            var Q68;
            Q68=makeQuery(id+"F8.imprint","IMPRINT",FACE,{"disambiguationData":[TD([[makeQuery(id+"F8.imprint","IMPRINT",EDGE,{"derivedFrom":sQuery(id+"F8.wireOp",EDGE,"E28.sketch_text.stroke-58")}),-1.0]])]});
            var Q69;
            Q69=makeQuery(id+"F8.imprint","IMPRINT",FACE,{"disambiguationData":[TD([[makeQuery(id+"F8.imprint","IMPRINT",EDGE,{"derivedFrom":sQuery(id+"F8.wireOp",EDGE,"E28.sketch_text.stroke-76")}),-1.0]])]});
            var Q70;
            Q70=makeQuery(id+"F8.imprint","IMPRINT",FACE,{"disambiguationData":[TD([[makeQuery(id+"F8.imprint","IMPRINT",EDGE,{"derivedFrom":sQuery(id+"F8.wireOp",EDGE,"E28.sketch_text.stroke-80")}),-1.0]])]});
            var Q71;
            Q71=makeQuery(id+"F8.imprint","IMPRINT",FACE,{"disambiguationData":[TD([[makeQuery(id+"F8.imprint","IMPRINT",EDGE,{"derivedFrom":sQuery(id+"F8.wireOp",EDGE,"E28.sketch_text.stroke-95")}),-1.0]])]});
            var Q72;
            Q72=makeQuery(id+"F8.imprint","IMPRINT",FACE,{"disambiguationData":[TD([[makeQuery(id+"F8.imprint","IMPRINT",EDGE,{"derivedFrom":sQuery(id+"F8.wireOp",EDGE,"E28.sketch_text.stroke-110")}),-1.0]])]});
            var Q73;
            Q73=makeQuery(id+"F8.imprint","IMPRINT",FACE,{"disambiguationData":[TD([[makeQuery(id+"F8.imprint","IMPRINT",EDGE,{"derivedFrom":sQuery(id+"F8.wireOp",EDGE,"E28.sketch_text.stroke-124")}),-1.0]])]});
            var Q74;
            Q74=makeQuery(id+"F8.imprint","IMPRINT",FACE,{"disambiguationData":[TD([[makeQuery(id+"F8.imprint","IMPRINT",EDGE,{"derivedFrom":sQuery(id+"F8.wireOp",EDGE,"E33.sketch_text.stroke-0")}),-1.0]])]});
            var Q75;
            Q75=makeQuery(id+"F8.imprint","IMPRINT",FACE,{"disambiguationData":[TD([[makeQuery(id+"F8.imprint","IMPRINT",EDGE,{"derivedFrom":sQuery(id+"F8.wireOp",EDGE,"E33.sketch_text.stroke-15")}),-1.0]])]});
            var Q76;
            Q76=makeQuery(id+"F8.imprint","IMPRINT",FACE,{"disambiguationData":[TD([[makeQuery(id+"F8.imprint","IMPRINT",EDGE,{"derivedFrom":sQuery(id+"F8.wireOp",EDGE,"E33.sketch_text.stroke-31")}),-1.0]])]});
            var Q77;
            Q77=makeQuery(id+"F8.imprint","IMPRINT",FACE,{"disambiguationData":[TD([[makeQuery(id+"F8.imprint","IMPRINT",EDGE,{"derivedFrom":sQuery(id+"F8.wireOp",EDGE,"E33.sketch_text.stroke-51")}),-1.0]])]});
            var Q78;
            Q78=makeQuery(id+"F8.imprint","IMPRINT",FACE,{"disambiguationData":[TD([[makeQuery(id+"F8.imprint","IMPRINT",EDGE,{"derivedFrom":sQuery(id+"F8.wireOp",EDGE,"E33.sketch_text.stroke-63")}),-1.0]])]});
            var Q79;
            Q79=makeQuery(id+"F8.imprint","IMPRINT",FACE,{"disambiguationData":[TD([[makeQuery(id+"F8.imprint","IMPRINT",EDGE,{"derivedFrom":sQuery(id+"F8.wireOp",EDGE,"E34.sketch_text.stroke-0")}),-1.0]])]});
            var Q80;
            Q80=makeQuery(id+"F8.imprint","IMPRINT",FACE,{"disambiguationData":[TD([[makeQuery(id+"F8.imprint","IMPRINT",EDGE,{"derivedFrom":sQuery(id+"F8.wireOp",EDGE,"E34.sketch_text.stroke-25")}),-1.0]])]});
            var Q81;
            Q81=makeQuery(id+"F8.imprint","IMPRINT",FACE,{"disambiguationData":[TD([[makeQuery(id+"F8.imprint","IMPRINT",EDGE,{"derivedFrom":sQuery(id+"F8.wireOp",EDGE,"E34.sketch_text.stroke-29")}),-1.0]])]});
            var Q82;
            Q82=makeQuery(id+"F8.imprint","IMPRINT",FACE,{"disambiguationData":[TD([[makeQuery(id+"F8.imprint","IMPRINT",EDGE,{"derivedFrom":sQuery(id+"F8.wireOp",EDGE,"E34.sketch_text.stroke-43")}),-1.0]])]});
            var Q83;
            Q83=makeQuery(id+"F8.imprint","IMPRINT",FACE,{"disambiguationData":[TD([[makeQuery(id+"F8.imprint","IMPRINT",EDGE,{"derivedFrom":sQuery(id+"F8.wireOp",EDGE,"E34.sketch_text.stroke-55")}),-1.0]])]});
            var Q84;
            Q84=makeQuery(id+"F8.imprint","IMPRINT",FACE,{"disambiguationData":[TD([[makeQuery(id+"F8.imprint","IMPRINT",EDGE,{"derivedFrom":sQuery(id+"F8.wireOp",EDGE,"E34.sketch_text.stroke-70")}),-1.0]])]});
            var Q85;
            Q85=makeQuery(id+"F8.imprint","IMPRINT",FACE,{"disambiguationData":[TD([[makeQuery(id+"F8.imprint","IMPRINT",EDGE,{"derivedFrom":sQuery(id+"F8.wireOp",EDGE,"E34.sketch_text.stroke-83")}),-1.0]])]});
            var Q86;
            Q86=makeQuery(id+"F8.imprint","IMPRINT",FACE,{"disambiguationData":[TD([[makeQuery(id+"F8.imprint","IMPRINT",EDGE,{"derivedFrom":sQuery(id+"F8.wireOp",EDGE,"E34.sketch_text.stroke-101")}),-1.0]])]});
            var Q87;
            Q87=makeQuery(id+"F8.imprint","IMPRINT",FACE,{"disambiguationData":[TD([[makeQuery(id+"F8.imprint","IMPRINT",EDGE,{"derivedFrom":sQuery(id+"F8.wireOp",EDGE,"E34.sketch_text.stroke-113")}),-1.0]])]});
            var Q88;
            Q88=makeQuery(id+"F8.imprint","IMPRINT",FACE,{"disambiguationData":[TD([[makeQuery(id+"F8.imprint","IMPRINT",EDGE,{"derivedFrom":sQuery(id+"F8.wireOp",EDGE,"E34.sketch_text.stroke-131")}),-1.0]])]});
            var Q89;
            Q89=makeQuery(id+"F8.imprint","IMPRINT",FACE,{"disambiguationData":[TD([[makeQuery(id+"F8.imprint","IMPRINT",EDGE,{"derivedFrom":sQuery(id+"F8.wireOp",EDGE,"E34.sketch_text.stroke-144")}),-1.0]])]});
            var Q90;
            Q90=makeQuery(id+"F8.imprint","IMPRINT",FACE,{"disambiguationData":[TD([[makeQuery(id+"F8.imprint","IMPRINT",EDGE,{"derivedFrom":sQuery(id+"F8.wireOp",EDGE,"E34.sketch_text.stroke-148")}),-1.0]])]});
            var Q91;
            Q91=makeQuery(id+"F8.imprint","IMPRINT",FACE,{"disambiguationData":[TD([[makeQuery(id+"F8.imprint","IMPRINT",EDGE,{"derivedFrom":sQuery(id+"F8.wireOp",EDGE,"E34.sketch_text.stroke-163")}),-1.0]])]});
            var Q92;
            Q92=makeQuery(id+"F8.imprint","IMPRINT",FACE,{"disambiguationData":[TD([[makeQuery(id+"F8.imprint","IMPRINT",EDGE,{"derivedFrom":sQuery(id+"F8.wireOp",EDGE,"E34.sketch_text.stroke-178")}),-1.0]])]});
            var Q93;
            Q93=makeQuery(id+"F8.imprint","IMPRINT",FACE,{"disambiguationData":[TD([[makeQuery(id+"F8.imprint","IMPRINT",EDGE,{"derivedFrom":sQuery(id+"F8.wireOp",EDGE,"E34.sketch_text.stroke-192")}),-1.0]])]});
            var Q94;
            Q94=makeQuery(id+"F8.imprint","IMPRINT",FACE,{"disambiguationData":[TD([[makeQuery(id+"F8.imprint","IMPRINT",EDGE,{"derivedFrom":sQuery(id+"F8.wireOp",EDGE,"E35.sketch_text.stroke-0")}),-1.0]])]});
            var Q95;
            Q95=makeQuery(id+"F8.imprint","IMPRINT",FACE,{"disambiguationData":[TD([[makeQuery(id+"F8.imprint","IMPRINT",EDGE,{"derivedFrom":sQuery(id+"F8.wireOp",EDGE,"E35.sketch_text.stroke-20")}),-1.0]])]});
            var Q96;
            Q96=makeQuery(id+"F8.imprint","IMPRINT",FACE,{"disambiguationData":[TD([[makeQuery(id+"F8.imprint","IMPRINT",EDGE,{"derivedFrom":sQuery(id+"F8.wireOp",EDGE,"E35.sketch_text.stroke-35")}),-1.0]])]});
            extrude(context, id + "F9", {"entities" : qUnion([Q0, Q1, Q2, Q3, Q4, Q5, Q6, Q7, Q8, Q9, Q10, Q11, Q12, Q13, Q14, Q15, Q16, Q17, Q18, Q19, Q20, Q21, Q22, Q23, Q24, Q25, Q26, Q27, Q28, Q29, Q30, Q31, Q32, Q33, Q34, Q35, Q36, Q37, Q38, Q39, Q40, Q41, Q42, Q43, Q44, Q45, Q46, Q47, Q48, Q49, Q50, Q51, Q52, Q53, Q54, Q55, Q56, Q57, Q58, Q59, Q60, Q61, Q62, Q63, Q64, Q65, Q66, Q67, Q68, Q69, Q70, Q71, Q72, Q73, Q74, Q75, Q76, Q77, Q78, Q79, Q80, Q81, Q82, Q83, Q84, Q85, Q86, Q87, Q88, Q89, Q90, Q91, Q92, Q93, Q94, Q95, Q96]), "operationType" : NewBodyOperationType.REMOVE, "oppositeDirection" : true, "depth" : 1 * mm, "offsetDistance" : 25 * mm});
        }
        {
            var Q0;
            Q0=makeQuery(id+"F1.opExtrude","CAP_FACE",FACE,{"disambiguationData":[OSD([sQuery(id+"F0.wireOp",EDGE,"E0.bottom"),sQuery(id+"F0.wireOp",EDGE,"E0.top"),sQuery(id+"F0.wireOp",EDGE,"E0.left"),sQuery(id+"F0.wireOp",EDGE,"E0.right")])],"isStart":false});
            var sketch = newSketch(context, id + "F10", { "sketchPlane" : qUnion([Q0])});
            skPoint(sketch, "E36", {"position": v(-66.95, 99) * mm});
            skPoint(sketch, "E37", {"position": v(-66.95, 30) * mm});
            skPoint(sketch, "E38", {"position": v(13.95, 99) * mm});
            skPoint(sketch, "E39", {"position": v(13.95, 30) * mm});
            skCircle(sketch, "E40", {"center": v(-66.95, 99) * mm, "radius": 2.65 * mm});
            skCircle(sketch, "E41", {"center": v(13.95, 99) * mm, "radius": 2.65 * mm});
            skCircle(sketch, "E42", {"center": v(13.95, 30) * mm, "radius": 2.65 * mm});
            skCircle(sketch, "E43", {"center": v(-66.95, 30) * mm, "radius": 2.65 * mm});
            skPoint(sketch, "E44", {"position": v(-67.5, -30.5) * mm});
            skPoint(sketch, "E45", {"position": v(66.5, -30.5) * mm});
            skPoint(sketch, "E46", {"position": v(65.5, -96.5) * mm});
            skPoint(sketch, "E47", {"position": v(-66.5, -96.5) * mm});
            skCircle(sketch, "E48", {"center": v(-67.5, -30.5) * mm, "radius": 2.65 * mm});
            skCircle(sketch, "E49", {"center": v(66.5, -30.5) * mm, "radius": 2.65 * mm});
            skCircle(sketch, "E50", {"center": v(65.5, -96.5) * mm, "radius": 2.65 * mm});
            skCircle(sketch, "E51", {"center": v(-66.5, -96.5) * mm, "radius": 2.65 * mm});
            skPoint(sketch, "E52", {"position": v(65.5, -30.5) * mm});
            skSolve(sketch);
        }
        {
            var Q0;
            Q0=makeQuery(id+"F10.imprint","IMPRINT",FACE,{"disambiguationData":[TD([[makeQuery(id+"F10.imprint","IMPRINT",EDGE,{"derivedFrom":sQuery(id+"F10.wireOp",EDGE,"E40")}),1.0]])]});
            var Q1;
            Q1=makeQuery(id+"F10.imprint","IMPRINT",FACE,{"disambiguationData":[TD([[makeQuery(id+"F10.imprint","IMPRINT",EDGE,{"derivedFrom":sQuery(id+"F10.wireOp",EDGE,"E43")}),1.0]])]});
            var Q2;
            Q2=makeQuery(id+"F10.imprint","IMPRINT",FACE,{"disambiguationData":[TD([[makeQuery(id+"F10.imprint","IMPRINT",EDGE,{"derivedFrom":sQuery(id+"F10.wireOp",EDGE,"E42")}),1.0]])]});
            var Q3;
            Q3=makeQuery(id+"F10.imprint","IMPRINT",FACE,{"disambiguationData":[TD([[makeQuery(id+"F10.imprint","IMPRINT",EDGE,{"derivedFrom":sQuery(id+"F10.wireOp",EDGE,"E41")}),1.0]])]});
            var Q4;
            Q4=makeQuery(id+"F10.imprint","IMPRINT",FACE,{"disambiguationData":[TD([[makeQuery(id+"F10.imprint","IMPRINT",EDGE,{"derivedFrom":sQuery(id+"F10.wireOp",EDGE,"E48")}),1.0]])]});
            var Q5;
            Q5=makeQuery(id+"F10.imprint","IMPRINT",FACE,{"disambiguationData":[TD([[makeQuery(id+"F10.imprint","IMPRINT",EDGE,{"derivedFrom":sQuery(id+"F10.wireOp",EDGE,"E49")}),1.0]])]});
            var Q6;
            Q6=makeQuery(id+"F10.imprint","IMPRINT",FACE,{"disambiguationData":[TD([[makeQuery(id+"F10.imprint","IMPRINT",EDGE,{"derivedFrom":sQuery(id+"F10.wireOp",EDGE,"E50")}),1.0]])]});
            var Q7;
            Q7=makeQuery(id+"F10.imprint","IMPRINT",FACE,{"disambiguationData":[TD([[makeQuery(id+"F10.imprint","IMPRINT",EDGE,{"derivedFrom":sQuery(id+"F10.wireOp",EDGE,"E51")}),1.0]])]});
            extrude(context, id + "F11", {"entities" : qUnion([Q0, Q1, Q2, Q3, Q4, Q5, Q6, Q7]), "operationType" : NewBodyOperationType.REMOVE, "oppositeDirection" : true, "depth" : 6.2 * mm, "offsetDistance" : 25 * mm});
        }
        {
            var Q0;
            Q0=makeQuery(id+"F2.opExtrude","SWEPT_FACE",FACE,{"disambiguationData":[OSD([sQuery(id+"F0.wireOp",EDGE,"E1.left")])]});
            var sketch = newSketch(context, id + "F12", { "sketchPlane" : qUnion([Q0])});
            skText(sketch, "E53", { "text": "Sentinel One", "fontName": "OpenSans-Italic.ttf"});
            const initialGuessF12  = {"E53": [-0.0995, 0.0715, 1, 0, 0.014]};
            skSetInitialGuess(sketch, initialGuessF12);
            skSolve(sketch);
        }
        {
            var Q0;
            Q0=makeQuery(id+"F12.imprint","IMPRINT",FACE,{"disambiguationData":[TD([[makeQuery(id+"F12.imprint","IMPRINT",EDGE,{"derivedFrom":sQuery(id+"F12.wireOp",EDGE,"E53.sketch_text.stroke-0")}),-1.0]])]});
            var Q1;
            Q1=makeQuery(id+"F12.imprint","IMPRINT",FACE,{"disambiguationData":[TD([[makeQuery(id+"F12.imprint","IMPRINT",EDGE,{"derivedFrom":sQuery(id+"F12.wireOp",EDGE,"E53.sketch_text.stroke-27")}),-1.0]])]});
            var Q2;
            Q2=makeQuery(id+"F12.imprint","IMPRINT",FACE,{"disambiguationData":[TD([[makeQuery(id+"F12.imprint","IMPRINT",EDGE,{"derivedFrom":sQuery(id+"F12.wireOp",EDGE,"E53.sketch_text.stroke-52")}),-1.0]])]});
            var Q3;
            Q3=makeQuery(id+"F12.imprint","IMPRINT",FACE,{"disambiguationData":[TD([[makeQuery(id+"F12.imprint","IMPRINT",EDGE,{"derivedFrom":sQuery(id+"F12.wireOp",EDGE,"E53.sketch_text.stroke-72")}),-1.0]])]});
            var Q4;
            Q4=makeQuery(id+"F12.imprint","IMPRINT",FACE,{"disambiguationData":[TD([[makeQuery(id+"F12.imprint","IMPRINT",EDGE,{"derivedFrom":sQuery(id+"F12.wireOp",EDGE,"E53.sketch_text.stroke-93")}),-1.0]])]});
            var Q5;
            Q5=makeQuery(id+"F12.imprint","IMPRINT",FACE,{"disambiguationData":[TD([[makeQuery(id+"F12.imprint","IMPRINT",EDGE,{"derivedFrom":sQuery(id+"F12.wireOp",EDGE,"E53.sketch_text.stroke-97")}),-1.0]])]});
            var Q6;
            Q6=makeQuery(id+"F12.imprint","IMPRINT",FACE,{"disambiguationData":[TD([[makeQuery(id+"F12.imprint","IMPRINT",EDGE,{"derivedFrom":sQuery(id+"F12.wireOp",EDGE,"E53.sketch_text.stroke-104")}),-1.0]])]});
            var Q7;
            Q7=makeQuery(id+"F12.imprint","IMPRINT",FACE,{"disambiguationData":[TD([[makeQuery(id+"F12.imprint","IMPRINT",EDGE,{"derivedFrom":sQuery(id+"F12.wireOp",EDGE,"E53.sketch_text.stroke-124")}),-1.0]])]});
            var Q8;
            Q8=makeQuery(id+"F12.imprint","IMPRINT",FACE,{"disambiguationData":[TD([[makeQuery(id+"F12.imprint","IMPRINT",EDGE,{"derivedFrom":sQuery(id+"F12.wireOp",EDGE,"E53.sketch_text.stroke-149")}),-1.0]])]});
            var Q9;
            Q9=makeQuery(id+"F12.imprint","IMPRINT",FACE,{"disambiguationData":[TD([[makeQuery(id+"F12.imprint","IMPRINT",EDGE,{"derivedFrom":sQuery(id+"F12.wireOp",EDGE,"E53.sketch_text.stroke-153")}),-1.0]])]});
            var Q10;
            Q10=makeQuery(id+"F12.imprint","IMPRINT",FACE,{"disambiguationData":[TD([[makeQuery(id+"F12.imprint","IMPRINT",EDGE,{"derivedFrom":sQuery(id+"F12.wireOp",EDGE,"E53.sketch_text.stroke-173")}),-1.0]])]});
            var Q11;
            Q11=makeQuery(id+"F12.imprint","IMPRINT",FACE,{"disambiguationData":[TD([[makeQuery(id+"F12.imprint","IMPRINT",EDGE,{"derivedFrom":sQuery(id+"F12.wireOp",EDGE,"E53.sketch_text.stroke-193")}),-1.0]])]});
            extrude(context, id + "F13", {"entities" : qUnion([Q0, Q1, Q2, Q3, Q4, Q5, Q6, Q7, Q8, Q9, Q10, Q11]), "operationType" : NewBodyOperationType.REMOVE, "oppositeDirection" : true, "depth" : 1 * mm, "offsetDistance" : 25 * mm});
        }
        {
            var Q0;
            Q0=makeQuery(id+"F3.imprint","IMPRINT",FACE,{"disambiguationData":[TD([[makeQuery(id+"F3.imprint","IMPRINT",EDGE,{"derivedFrom":sQuery(id+"F3.wireOp",EDGE,"E14")}),1.0]])]});
            extrude(context, id + "F14", {"entities" : qUnion([Q0]), "operationType" : NewBodyOperationType.REMOVE, "endBound" : BoundingType.UP_TO_NEXT, "oppositeDirection" : true, "depth" : 25 * mm, "offsetDistance" : 25 * mm});
        }
        {
            var Q0;
            Q0=makeQuery(id+"F2.opExtrude","CAP_FACE",FACE,{"disambiguationData":[OSD([sQuery(id+"F0.wireOp",EDGE,"E0.bottom"),sQuery(id+"F0.wireOp",EDGE,"E0.top"),sQuery(id+"F0.wireOp",EDGE,"E0.left"),sQuery(id+"F0.wireOp",EDGE,"E0.right"),sQuery(id+"F0.wireOp",EDGE,"E1.bottom"),sQuery(id+"F0.wireOp",EDGE,"E1.top"),sQuery(id+"F0.wireOp",EDGE,"E1.left"),sQuery(id+"F0.wireOp",EDGE,"E1.right")])],"isStart":false});
            var sketch = newSketch(context, id + "F15", { "sketchPlane" : qUnion([Q0])});
            skCircle(sketch, "E54", {"center": v(-75, 105) * mm, "radius": 17.5 * mm});
            skCircle(sketch, "E55", {"center": v(75, 105) * mm, "radius": 17.5 * mm});
            skCircle(sketch, "E56", {"center": v(75, -105) * mm, "radius": 17.5 * mm});
            skCircle(sketch, "E57", {"center": v(-75, -105) * mm, "radius": 17.5 * mm});
            skSolve(sketch);
        }
        {
            var Q0;
            {var subQ0=sQuery(id+"F15.wireOp",EDGE,"E54");var subQ1=makeQuery(id+"F2.opExtrude","CAP_EDGE",EDGE,{"disambiguationData":[OSD([sQuery(id+"F0.wireOp",EDGE,"E0.top")])],"isStart":false});var subQ2=makeQuery(id+"F15.imprint","INTERSECT",VERTEX,{"derivedFrom":[subQ1,subQ0]});Q0=makeQuery(id+"F15.imprint","IMPRINT",FACE,{"disambiguationData":[TD([[makeQuery(id+"F15.imprint","IMPRINT",EDGE,{"disambiguationData":[TD([[subQ2,1.0]])],"derivedFrom":subQ0}),1.0]])]});}
            var Q1;
            {var subQ0=sQuery(id+"F15.wireOp",EDGE,"E55");var subQ1=makeQuery(id+"F2.opExtrude","CAP_EDGE",EDGE,{"disambiguationData":[OSD([sQuery(id+"F0.wireOp",EDGE,"E0.top")])],"isStart":false});var subQ2=makeQuery(id+"F15.imprint","INTERSECT",VERTEX,{"derivedFrom":[subQ1,subQ0]});Q1=makeQuery(id+"F15.imprint","IMPRINT",FACE,{"disambiguationData":[TD([[makeQuery(id+"F15.imprint","IMPRINT",EDGE,{"disambiguationData":[TD([[subQ2,-1.0]])],"derivedFrom":subQ0}),1.0]])]});}
            var Q2;
            {var subQ0=sQuery(id+"F15.wireOp",EDGE,"E56");var subQ1=makeQuery(id+"F2.opExtrude","CAP_EDGE",EDGE,{"disambiguationData":[OSD([sQuery(id+"F0.wireOp",EDGE,"E0.left")])],"isStart":false});var subQ2=makeQuery(id+"F15.imprint","INTERSECT",VERTEX,{"derivedFrom":[subQ1,subQ0]});Q2=makeQuery(id+"F15.imprint","IMPRINT",FACE,{"disambiguationData":[TD([[makeQuery(id+"F15.imprint","IMPRINT",EDGE,{"disambiguationData":[TD([[subQ2,-1.0]])],"derivedFrom":subQ0}),1.0]])]});}
            var Q3;
            {var subQ0=sQuery(id+"F15.wireOp",EDGE,"E57");var subQ1=makeQuery(id+"F2.opExtrude","CAP_EDGE",EDGE,{"disambiguationData":[OSD([sQuery(id+"F0.wireOp",EDGE,"E0.right")])],"isStart":false});var subQ2=makeQuery(id+"F15.imprint","INTERSECT",VERTEX,{"derivedFrom":[subQ1,subQ0]});Q3=makeQuery(id+"F15.imprint","IMPRINT",FACE,{"disambiguationData":[TD([[makeQuery(id+"F15.imprint","IMPRINT",EDGE,{"disambiguationData":[TD([[subQ2,1.0]])],"derivedFrom":subQ0}),1.0]])]});}
            extrude(context, id + "F16", {"entities" : qUnion([Q0, Q1, Q2, Q3]), "operationType" : NewBodyOperationType.ADD, "oppositeDirection" : true, "depth" : 8 * mm, "offsetDistance" : 25 * mm});
        }
        {
            var Q0;
            Q0=makeQuery(id+"F2.opExtrude","SWEPT_FACE",FACE,{"disambiguationData":[OSD([sQuery(id+"F0.wireOp",EDGE,"E1.bottom")])]});
            var sketch = newSketch(context, id + "F17", { "sketchPlane" : qUnion([Q0])});
            skCircle(sketch, "E58", {"center": v(-56.22, 80) * mm, "radius": 2.5 * mm});
            skCircle(sketch, "E59.0.1.0", {"center": v(-56.22, 67.5) * mm, "radius": 2.5 * mm});
            skCircle(sketch, "E59.0.2.0", {"center": v(-56.22, 55) * mm, "radius": 2.5 * mm});
            skCircle(sketch, "E59.0.3.0", {"center": v(-56.22, 42.5) * mm, "radius": 2.5 * mm});
            skCircle(sketch, "E59.0.4.0", {"center": v(-56.22, 30) * mm, "radius": 2.5 * mm});
            skCircle(sketch, "E59.0.5.0", {"center": v(-56.22, 17.5) * mm, "radius": 2.5 * mm});
            skCircle(sketch, "E59.1.0.0", {"center": v(-43.73, 80) * mm, "radius": 2.5 * mm});
            skCircle(sketch, "E59.1.1.0", {"center": v(-43.73, 67.5) * mm, "radius": 2.5 * mm});
            skCircle(sketch, "E59.1.2.0", {"center": v(-43.73, 55) * mm, "radius": 2.5 * mm});
            skCircle(sketch, "E59.1.3.0", {"center": v(-43.73, 42.5) * mm, "radius": 2.5 * mm});
            skCircle(sketch, "E59.1.4.0", {"center": v(-43.73, 30) * mm, "radius": 2.5 * mm});
            skCircle(sketch, "E59.1.5.0", {"center": v(-43.73, 17.5) * mm, "radius": 2.5 * mm});
            skCircle(sketch, "E59.2.0.0", {"center": v(-31.23, 80) * mm, "radius": 2.5 * mm});
            skCircle(sketch, "E59.2.1.0", {"center": v(-31.23, 67.5) * mm, "radius": 2.5 * mm});
            skCircle(sketch, "E59.2.2.0", {"center": v(-31.23, 55) * mm, "radius": 2.5 * mm});
            skCircle(sketch, "E59.2.3.0", {"center": v(-31.23, 42.5) * mm, "radius": 2.5 * mm});
            skCircle(sketch, "E59.2.4.0", {"center": v(-31.23, 30) * mm, "radius": 2.5 * mm});
            skCircle(sketch, "E59.2.5.0", {"center": v(-31.23, 17.5) * mm, "radius": 2.5 * mm});
            skCircle(sketch, "E59.3.0.0", {"center": v(-18.73, 80) * mm, "radius": 2.5 * mm});
            skCircle(sketch, "E59.3.1.0", {"center": v(-18.73, 67.5) * mm, "radius": 2.5 * mm});
            skCircle(sketch, "E59.3.2.0", {"center": v(-18.73, 55) * mm, "radius": 2.5 * mm});
            skCircle(sketch, "E59.3.3.0", {"center": v(-18.73, 42.5) * mm, "radius": 2.5 * mm});
            skCircle(sketch, "E59.3.4.0", {"center": v(-18.73, 30) * mm, "radius": 2.5 * mm});
            skCircle(sketch, "E59.3.5.0", {"center": v(-18.73, 17.5) * mm, "radius": 2.5 * mm});
            skCircle(sketch, "E59.4.0.0", {"center": v(-6.23, 80) * mm, "radius": 2.5 * mm});
            skCircle(sketch, "E59.4.1.0", {"center": v(-6.23, 67.5) * mm, "radius": 2.5 * mm});
            skCircle(sketch, "E59.4.2.0", {"center": v(-6.23, 55) * mm, "radius": 2.5 * mm});
            skCircle(sketch, "E59.4.3.0", {"center": v(-6.23, 42.5) * mm, "radius": 2.5 * mm});
            skCircle(sketch, "E59.4.4.0", {"center": v(-6.23, 30) * mm, "radius": 2.5 * mm});
            skCircle(sketch, "E59.4.5.0", {"center": v(-6.23, 17.5) * mm, "radius": 2.5 * mm});
            skCircle(sketch, "E59.5.0.0", {"center": v(6.27, 80) * mm, "radius": 2.5 * mm});
            skCircle(sketch, "E59.5.1.0", {"center": v(6.27, 67.5) * mm, "radius": 2.5 * mm});
            skCircle(sketch, "E59.5.2.0", {"center": v(6.27, 55) * mm, "radius": 2.5 * mm});
            skCircle(sketch, "E59.5.3.0", {"center": v(6.27, 42.5) * mm, "radius": 2.5 * mm});
            skCircle(sketch, "E59.5.4.0", {"center": v(6.27, 30) * mm, "radius": 2.5 * mm});
            skCircle(sketch, "E59.5.5.0", {"center": v(6.27, 17.5) * mm, "radius": 2.5 * mm});
            skCircle(sketch, "E59.6.0.0", {"center": v(18.77, 80) * mm, "radius": 2.5 * mm});
            skCircle(sketch, "E59.6.1.0", {"center": v(18.77, 67.5) * mm, "radius": 2.5 * mm});
            skCircle(sketch, "E59.6.2.0", {"center": v(18.77, 55) * mm, "radius": 2.5 * mm});
            skCircle(sketch, "E59.6.3.0", {"center": v(18.77, 42.5) * mm, "radius": 2.5 * mm});
            skCircle(sketch, "E59.6.4.0", {"center": v(18.77, 30) * mm, "radius": 2.5 * mm});
            skCircle(sketch, "E59.6.5.0", {"center": v(18.77, 17.5) * mm, "radius": 2.5 * mm});
            skCircle(sketch, "E59.7.0.0", {"center": v(31.27, 80) * mm, "radius": 2.5 * mm});
            skCircle(sketch, "E59.7.1.0", {"center": v(31.27, 67.5) * mm, "radius": 2.5 * mm});
            skCircle(sketch, "E59.7.2.0", {"center": v(31.27, 55) * mm, "radius": 2.5 * mm});
            skCircle(sketch, "E59.7.3.0", {"center": v(31.27, 42.5) * mm, "radius": 2.5 * mm});
            skCircle(sketch, "E59.7.4.0", {"center": v(31.27, 30) * mm, "radius": 2.5 * mm});
            skCircle(sketch, "E59.7.5.0", {"center": v(31.27, 17.5) * mm, "radius": 2.5 * mm});
            skCircle(sketch, "E59.8.0.0", {"center": v(43.77, 80) * mm, "radius": 2.5 * mm});
            skCircle(sketch, "E59.8.1.0", {"center": v(43.77, 67.5) * mm, "radius": 2.5 * mm});
            skCircle(sketch, "E59.8.2.0", {"center": v(43.77, 55) * mm, "radius": 2.5 * mm});
            skCircle(sketch, "E59.8.3.0", {"center": v(43.77, 42.5) * mm, "radius": 2.5 * mm});
            skCircle(sketch, "E59.8.4.0", {"center": v(43.77, 30) * mm, "radius": 2.5 * mm});
            skCircle(sketch, "E59.8.5.0", {"center": v(43.77, 17.5) * mm, "radius": 2.5 * mm});
            skCircle(sketch, "E59.9.0.0", {"center": v(56.27, 80) * mm, "radius": 2.5 * mm});
            skCircle(sketch, "E59.9.1.0", {"center": v(56.27, 67.5) * mm, "radius": 2.5 * mm});
            skCircle(sketch, "E59.9.2.0", {"center": v(56.27, 55) * mm, "radius": 2.5 * mm});
            skCircle(sketch, "E59.9.3.0", {"center": v(56.27, 42.5) * mm, "radius": 2.5 * mm});
            skCircle(sketch, "E59.9.4.0", {"center": v(56.27, 30) * mm, "radius": 2.5 * mm});
            skCircle(sketch, "E59.9.5.0", {"center": v(56.27, 17.5) * mm, "radius": 2.5 * mm});
            skLineSegment(sketch, "E59.direction1", {"start": v(-56.22, 80) * mm, "end": v(-43.73, 80) * mm, "construction": true});
            skLineSegment(sketch, "E59.direction2", {"start": v(-56.22, 80) * mm, "end": v(-56.22, 67.5) * mm, "construction": true});
            skSolve(sketch);
        }
        {
            var Q0;
            Q0=makeQuery(id+"F17.imprint","IMPRINT",FACE,{"disambiguationData":[TD([[makeQuery(id+"F17.imprint","IMPRINT",EDGE,{"derivedFrom":sQuery(id+"F17.wireOp",EDGE,"E59.4.3.0")}),1.0]])]});
            var Q1;
            Q1=makeQuery(id+"F17.imprint","IMPRINT",FACE,{"disambiguationData":[TD([[makeQuery(id+"F17.imprint","IMPRINT",EDGE,{"derivedFrom":sQuery(id+"F17.wireOp",EDGE,"E59.1.5.0")}),1.0]])]});
            var Q2;
            Q2=makeQuery(id+"F17.imprint","IMPRINT",FACE,{"disambiguationData":[TD([[makeQuery(id+"F17.imprint","IMPRINT",EDGE,{"derivedFrom":sQuery(id+"F17.wireOp",EDGE,"E59.5.5.0")}),1.0]])]});
            var Q3;
            Q3=makeQuery(id+"F17.imprint","IMPRINT",FACE,{"disambiguationData":[TD([[makeQuery(id+"F17.imprint","IMPRINT",EDGE,{"derivedFrom":sQuery(id+"F17.wireOp",EDGE,"E59.6.0.0")}),1.0]])]});
            var Q4;
            Q4=makeQuery(id+"F17.imprint","IMPRINT",FACE,{"disambiguationData":[TD([[makeQuery(id+"F17.imprint","IMPRINT",EDGE,{"derivedFrom":sQuery(id+"F17.wireOp",EDGE,"E59.6.4.0")}),1.0]])]});
            var Q5;
            Q5=makeQuery(id+"F17.imprint","IMPRINT",FACE,{"disambiguationData":[TD([[makeQuery(id+"F17.imprint","IMPRINT",EDGE,{"derivedFrom":sQuery(id+"F17.wireOp",EDGE,"E59.0.5.0")}),1.0]])]});
            var Q6;
            Q6=makeQuery(id+"F17.imprint","IMPRINT",FACE,{"disambiguationData":[TD([[makeQuery(id+"F17.imprint","IMPRINT",EDGE,{"derivedFrom":sQuery(id+"F17.wireOp",EDGE,"E59.6.6.0")}),1.0]])]});
            var Q7;
            Q7=makeQuery(id+"F17.imprint","IMPRINT",FACE,{"disambiguationData":[TD([[makeQuery(id+"F17.imprint","IMPRINT",EDGE,{"derivedFrom":sQuery(id+"F17.wireOp",EDGE,"E59.7.2.0")}),1.0]])]});
            var Q8;
            Q8=makeQuery(id+"F17.imprint","IMPRINT",FACE,{"disambiguationData":[TD([[makeQuery(id+"F17.imprint","IMPRINT",EDGE,{"derivedFrom":sQuery(id+"F17.wireOp",EDGE,"E59.7.5.0")}),1.0]])]});
            var Q9;
            Q9=makeQuery(id+"F17.imprint","IMPRINT",FACE,{"disambiguationData":[TD([[makeQuery(id+"F17.imprint","IMPRINT",EDGE,{"derivedFrom":sQuery(id+"F17.wireOp",EDGE,"E59.7.6.0")}),1.0]])]});
            var Q10;
            Q10=makeQuery(id+"F17.imprint","IMPRINT",FACE,{"disambiguationData":[TD([[makeQuery(id+"F17.imprint","IMPRINT",EDGE,{"derivedFrom":sQuery(id+"F17.wireOp",EDGE,"E59.6.5.0")}),1.0]])]});
            var Q11;
            Q11=makeQuery(id+"F17.imprint","IMPRINT",FACE,{"disambiguationData":[TD([[makeQuery(id+"F17.imprint","IMPRINT",EDGE,{"derivedFrom":sQuery(id+"F17.wireOp",EDGE,"E59.6.1.0")}),1.0]])]});
            var Q12;
            Q12=makeQuery(id+"F17.imprint","IMPRINT",FACE,{"disambiguationData":[TD([[makeQuery(id+"F17.imprint","IMPRINT",EDGE,{"derivedFrom":sQuery(id+"F17.wireOp",EDGE,"E59.2.3.0")}),1.0]])]});
            var Q13;
            Q13=makeQuery(id+"F17.imprint","IMPRINT",FACE,{"disambiguationData":[TD([[makeQuery(id+"F17.imprint","IMPRINT",EDGE,{"derivedFrom":sQuery(id+"F17.wireOp",EDGE,"E59.0.4.0")}),1.0]])]});
            var Q14;
            Q14=makeQuery(id+"F17.imprint","IMPRINT",FACE,{"disambiguationData":[TD([[makeQuery(id+"F17.imprint","IMPRINT",EDGE,{"derivedFrom":sQuery(id+"F17.wireOp",EDGE,"E59.8.3.0")}),1.0]])]});
            var Q15;
            Q15=makeQuery(id+"F17.imprint","IMPRINT",FACE,{"disambiguationData":[TD([[makeQuery(id+"F17.imprint","IMPRINT",EDGE,{"derivedFrom":sQuery(id+"F17.wireOp",EDGE,"E59.4.4.0")}),1.0]])]});
            var Q16;
            Q16=makeQuery(id+"F17.imprint","IMPRINT",FACE,{"disambiguationData":[TD([[makeQuery(id+"F17.imprint","IMPRINT",EDGE,{"derivedFrom":sQuery(id+"F17.wireOp",EDGE,"E59.6.3.0")}),1.0]])]});
            var Q17;
            Q17=makeQuery(id+"F17.imprint","IMPRINT",FACE,{"disambiguationData":[TD([[makeQuery(id+"F17.imprint","IMPRINT",EDGE,{"derivedFrom":sQuery(id+"F17.wireOp",EDGE,"E59.5.1.0")}),1.0]])]});
            var Q18;
            Q18=makeQuery(id+"F17.imprint","IMPRINT",FACE,{"disambiguationData":[TD([[makeQuery(id+"F17.imprint","IMPRINT",EDGE,{"derivedFrom":sQuery(id+"F17.wireOp",EDGE,"E59.7.1.0")}),1.0]])]});
            var Q19;
            Q19=makeQuery(id+"F17.imprint","IMPRINT",FACE,{"disambiguationData":[TD([[makeQuery(id+"F17.imprint","IMPRINT",EDGE,{"derivedFrom":sQuery(id+"F17.wireOp",EDGE,"E59.5.0.0")}),1.0]])]});
            var Q20;
            Q20=makeQuery(id+"F17.imprint","IMPRINT",FACE,{"disambiguationData":[TD([[makeQuery(id+"F17.imprint","IMPRINT",EDGE,{"derivedFrom":sQuery(id+"F17.wireOp",EDGE,"E59.2.4.0")}),1.0]])]});
            var Q21;
            Q21=makeQuery(id+"F17.imprint","IMPRINT",FACE,{"disambiguationData":[TD([[makeQuery(id+"F17.imprint","IMPRINT",EDGE,{"derivedFrom":sQuery(id+"F17.wireOp",EDGE,"E59.2.5.0")}),1.0]])]});
            var Q22;
            Q22=makeQuery(id+"F17.imprint","IMPRINT",FACE,{"disambiguationData":[TD([[makeQuery(id+"F17.imprint","IMPRINT",EDGE,{"derivedFrom":sQuery(id+"F17.wireOp",EDGE,"E59.3.3.0")}),1.0]])]});
            var Q23;
            Q23=makeQuery(id+"F17.imprint","IMPRINT",FACE,{"disambiguationData":[TD([[makeQuery(id+"F17.imprint","IMPRINT",EDGE,{"derivedFrom":sQuery(id+"F17.wireOp",EDGE,"E59.3.4.0")}),1.0]])]});
            var Q24;
            Q24=makeQuery(id+"F17.imprint","IMPRINT",FACE,{"disambiguationData":[TD([[makeQuery(id+"F17.imprint","IMPRINT",EDGE,{"derivedFrom":sQuery(id+"F17.wireOp",EDGE,"E59.9.4.0")}),1.0]])]});
            var Q25;
            Q25=makeQuery(id+"F17.imprint","IMPRINT",FACE,{"disambiguationData":[TD([[makeQuery(id+"F17.imprint","IMPRINT",EDGE,{"derivedFrom":sQuery(id+"F17.wireOp",EDGE,"E59.7.0.0")}),1.0]])]});
            var Q26;
            Q26=makeQuery(id+"F17.imprint","IMPRINT",FACE,{"disambiguationData":[TD([[makeQuery(id+"F17.imprint","IMPRINT",EDGE,{"derivedFrom":sQuery(id+"F17.wireOp",EDGE,"E59.5.2.0")}),1.0]])]});
            var Q27;
            Q27=makeQuery(id+"F17.imprint","IMPRINT",FACE,{"disambiguationData":[TD([[makeQuery(id+"F17.imprint","IMPRINT",EDGE,{"derivedFrom":sQuery(id+"F17.wireOp",EDGE,"E59.1.3.0")}),1.0]])]});
            var Q28;
            Q28=makeQuery(id+"F17.imprint","IMPRINT",FACE,{"disambiguationData":[TD([[makeQuery(id+"F17.imprint","IMPRINT",EDGE,{"derivedFrom":sQuery(id+"F17.wireOp",EDGE,"E59.4.2.0")}),1.0]])]});
            var Q29;
            Q29=makeQuery(id+"F17.imprint","IMPRINT",FACE,{"disambiguationData":[TD([[makeQuery(id+"F17.imprint","IMPRINT",EDGE,{"derivedFrom":sQuery(id+"F17.wireOp",EDGE,"E59.6.2.0")}),1.0]])]});
            var Q30;
            Q30=makeQuery(id+"F17.imprint","IMPRINT",FACE,{"disambiguationData":[TD([[makeQuery(id+"F17.imprint","IMPRINT",EDGE,{"derivedFrom":sQuery(id+"F17.wireOp",EDGE,"E59.9.5.0")}),1.0]])]});
            var Q31;
            Q31=makeQuery(id+"F17.imprint","IMPRINT",FACE,{"disambiguationData":[TD([[makeQuery(id+"F17.imprint","IMPRINT",EDGE,{"derivedFrom":sQuery(id+"F17.wireOp",EDGE,"E59.0.3.0")}),1.0]])]});
            var Q32;
            Q32=makeQuery(id+"F17.imprint","IMPRINT",FACE,{"disambiguationData":[TD([[makeQuery(id+"F17.imprint","IMPRINT",EDGE,{"derivedFrom":sQuery(id+"F17.wireOp",EDGE,"E59.8.2.0")}),1.0]])]});
            var Q33;
            Q33=makeQuery(id+"F17.imprint","IMPRINT",FACE,{"disambiguationData":[TD([[makeQuery(id+"F17.imprint","IMPRINT",EDGE,{"derivedFrom":sQuery(id+"F17.wireOp",EDGE,"E59.4.5.0")}),1.0]])]});
            var Q34;
            Q34=makeQuery(id+"F17.imprint","IMPRINT",FACE,{"disambiguationData":[TD([[makeQuery(id+"F17.imprint","IMPRINT",EDGE,{"derivedFrom":sQuery(id+"F17.wireOp",EDGE,"E59.8.5.0")}),1.0]])]});
            var Q35;
            Q35=makeQuery(id+"F17.imprint","IMPRINT",FACE,{"disambiguationData":[TD([[makeQuery(id+"F17.imprint","IMPRINT",EDGE,{"derivedFrom":sQuery(id+"F17.wireOp",EDGE,"E59.7.4.0")}),1.0]])]});
            var Q36;
            Q36=makeQuery(id+"F17.imprint","IMPRINT",FACE,{"disambiguationData":[TD([[makeQuery(id+"F17.imprint","IMPRINT",EDGE,{"derivedFrom":sQuery(id+"F17.wireOp",EDGE,"E59.7.3.0")}),1.0]])]});
            var Q37;
            Q37=makeQuery(id+"F17.imprint","IMPRINT",FACE,{"disambiguationData":[TD([[makeQuery(id+"F17.imprint","IMPRINT",EDGE,{"derivedFrom":sQuery(id+"F17.wireOp",EDGE,"E59.9.3.0")}),1.0]])]});
            var Q38;
            Q38=makeQuery(id+"F17.imprint","IMPRINT",FACE,{"disambiguationData":[TD([[makeQuery(id+"F17.imprint","IMPRINT",EDGE,{"derivedFrom":sQuery(id+"F17.wireOp",EDGE,"E59.3.5.0")}),1.0]])]});
            var Q39;
            Q39=makeQuery(id+"F17.imprint","IMPRINT",FACE,{"disambiguationData":[TD([[makeQuery(id+"F17.imprint","IMPRINT",EDGE,{"derivedFrom":sQuery(id+"F17.wireOp",EDGE,"E59.5.3.0")}),1.0]])]});
            var Q40;
            Q40=makeQuery(id+"F17.imprint","IMPRINT",FACE,{"disambiguationData":[TD([[makeQuery(id+"F17.imprint","IMPRINT",EDGE,{"derivedFrom":sQuery(id+"F17.wireOp",EDGE,"E59.1.4.0")}),1.0]])]});
            var Q41;
            Q41=makeQuery(id+"F17.imprint","IMPRINT",FACE,{"disambiguationData":[TD([[makeQuery(id+"F17.imprint","IMPRINT",EDGE,{"derivedFrom":sQuery(id+"F17.wireOp",EDGE,"E59.8.4.0")}),1.0]])]});
            var Q42;
            Q42=makeQuery(id+"F17.imprint","IMPRINT",FACE,{"disambiguationData":[TD([[makeQuery(id+"F17.imprint","IMPRINT",EDGE,{"derivedFrom":sQuery(id+"F17.wireOp",EDGE,"E59.5.4.0")}),1.0]])]});
            var Q43;
            Q43=makeQuery(id+"F17.imprint","IMPRINT",FACE,{"disambiguationData":[TD([[makeQuery(id+"F17.imprint","IMPRINT",EDGE,{"derivedFrom":sQuery(id+"F17.wireOp",EDGE,"E59.5.6.0")}),1.0]])]});
            var Q44;
            Q44=makeQuery(id+"F17.imprint","IMPRINT",FACE,{"disambiguationData":[TD([[makeQuery(id+"F17.imprint","IMPRINT",EDGE,{"derivedFrom":sQuery(id+"F17.wireOp",EDGE,"E59.2.1.0")}),1.0]])]});
            var Q45;
            Q45=makeQuery(id+"F17.imprint","IMPRINT",FACE,{"disambiguationData":[TD([[makeQuery(id+"F17.imprint","IMPRINT",EDGE,{"derivedFrom":sQuery(id+"F17.wireOp",EDGE,"E59.9.1.0")}),1.0]])]});
            var Q46;
            Q46=makeQuery(id+"F17.imprint","IMPRINT",FACE,{"disambiguationData":[TD([[makeQuery(id+"F17.imprint","IMPRINT",EDGE,{"derivedFrom":sQuery(id+"F17.wireOp",EDGE,"E59.2.2.0")}),1.0]])]});
            var Q47;
            Q47=makeQuery(id+"F17.imprint","IMPRINT",FACE,{"disambiguationData":[TD([[makeQuery(id+"F17.imprint","IMPRINT",EDGE,{"derivedFrom":sQuery(id+"F17.wireOp",EDGE,"E59.1.2.0")}),1.0]])]});
            var Q48;
            Q48=makeQuery(id+"F17.imprint","IMPRINT",FACE,{"disambiguationData":[TD([[makeQuery(id+"F17.imprint","IMPRINT",EDGE,{"derivedFrom":sQuery(id+"F17.wireOp",EDGE,"E59.9.2.0")}),1.0]])]});
            var Q49;
            Q49=makeQuery(id+"F17.imprint","IMPRINT",FACE,{"disambiguationData":[TD([[makeQuery(id+"F17.imprint","IMPRINT",EDGE,{"derivedFrom":sQuery(id+"F17.wireOp",EDGE,"E59.1.6.0")}),1.0]])]});
            var Q50;
            Q50=makeQuery(id+"F17.imprint","IMPRINT",FACE,{"disambiguationData":[TD([[makeQuery(id+"F17.imprint","IMPRINT",EDGE,{"derivedFrom":sQuery(id+"F17.wireOp",EDGE,"E59.1.1.0")}),1.0]])]});
            var Q51;
            Q51=makeQuery(id+"F17.imprint","IMPRINT",FACE,{"disambiguationData":[TD([[makeQuery(id+"F17.imprint","IMPRINT",EDGE,{"derivedFrom":sQuery(id+"F17.wireOp",EDGE,"E59.4.1.0")}),1.0]])]});
            var Q52;
            Q52=makeQuery(id+"F17.imprint","IMPRINT",FACE,{"disambiguationData":[TD([[makeQuery(id+"F17.imprint","IMPRINT",EDGE,{"derivedFrom":sQuery(id+"F17.wireOp",EDGE,"E59.9.0.0")}),1.0]])]});
            var Q53;
            Q53=makeQuery(id+"F17.imprint","IMPRINT",FACE,{"disambiguationData":[TD([[makeQuery(id+"F17.imprint","IMPRINT",EDGE,{"derivedFrom":sQuery(id+"F17.wireOp",EDGE,"E59.3.0.0")}),1.0]])]});
            var Q54;
            Q54=makeQuery(id+"F17.imprint","IMPRINT",FACE,{"disambiguationData":[TD([[makeQuery(id+"F17.imprint","IMPRINT",EDGE,{"derivedFrom":sQuery(id+"F17.wireOp",EDGE,"E59.0.6.0")}),1.0]])]});
            var Q55;
            Q55=makeQuery(id+"F17.imprint","IMPRINT",FACE,{"disambiguationData":[TD([[makeQuery(id+"F17.imprint","IMPRINT",EDGE,{"derivedFrom":sQuery(id+"F17.wireOp",EDGE,"E59.4.6.0")}),1.0]])]});
            var Q56;
            Q56=makeQuery(id+"F17.imprint","IMPRINT",FACE,{"disambiguationData":[TD([[makeQuery(id+"F17.imprint","IMPRINT",EDGE,{"derivedFrom":sQuery(id+"F17.wireOp",EDGE,"E59.3.2.0")}),1.0]])]});
            var Q57;
            Q57=makeQuery(id+"F17.imprint","IMPRINT",FACE,{"disambiguationData":[TD([[makeQuery(id+"F17.imprint","IMPRINT",EDGE,{"derivedFrom":sQuery(id+"F17.wireOp",EDGE,"E59.8.6.0")}),1.0]])]});
            var Q58;
            Q58=makeQuery(id+"F17.imprint","IMPRINT",FACE,{"disambiguationData":[TD([[makeQuery(id+"F17.imprint","IMPRINT",EDGE,{"derivedFrom":sQuery(id+"F17.wireOp",EDGE,"E59.3.1.0")}),1.0]])]});
            var Q59;
            Q59=makeQuery(id+"F17.imprint","IMPRINT",FACE,{"disambiguationData":[TD([[makeQuery(id+"F17.imprint","IMPRINT",EDGE,{"derivedFrom":sQuery(id+"F17.wireOp",EDGE,"E59.8.1.0")}),1.0]])]});
            var Q60;
            Q60=makeQuery(id+"F17.imprint","IMPRINT",FACE,{"disambiguationData":[TD([[makeQuery(id+"F17.imprint","IMPRINT",EDGE,{"derivedFrom":sQuery(id+"F17.wireOp",EDGE,"E58")}),1.0]])]});
            var Q61;
            Q61=makeQuery(id+"F17.imprint","IMPRINT",FACE,{"disambiguationData":[TD([[makeQuery(id+"F17.imprint","IMPRINT",EDGE,{"derivedFrom":sQuery(id+"F17.wireOp",EDGE,"E59.4.0.0")}),1.0]])]});
            var Q62;
            Q62=makeQuery(id+"F17.imprint","IMPRINT",FACE,{"disambiguationData":[TD([[makeQuery(id+"F17.imprint","IMPRINT",EDGE,{"derivedFrom":sQuery(id+"F17.wireOp",EDGE,"E59.9.6.0")}),1.0]])]});
            var Q63;
            Q63=makeQuery(id+"F17.imprint","IMPRINT",FACE,{"disambiguationData":[TD([[makeQuery(id+"F17.imprint","IMPRINT",EDGE,{"derivedFrom":sQuery(id+"F17.wireOp",EDGE,"E59.2.0.0")}),1.0]])]});
            var Q64;
            Q64=makeQuery(id+"F17.imprint","IMPRINT",FACE,{"disambiguationData":[TD([[makeQuery(id+"F17.imprint","IMPRINT",EDGE,{"derivedFrom":sQuery(id+"F17.wireOp",EDGE,"E59.3.6.0")}),1.0]])]});
            var Q65;
            Q65=makeQuery(id+"F17.imprint","IMPRINT",FACE,{"disambiguationData":[TD([[makeQuery(id+"F17.imprint","IMPRINT",EDGE,{"derivedFrom":sQuery(id+"F17.wireOp",EDGE,"E59.0.2.0")}),1.0]])]});
            var Q66;
            Q66=makeQuery(id+"F17.imprint","IMPRINT",FACE,{"disambiguationData":[TD([[makeQuery(id+"F17.imprint","IMPRINT",EDGE,{"derivedFrom":sQuery(id+"F17.wireOp",EDGE,"E59.0.1.0")}),1.0]])]});
            var Q67;
            Q67=makeQuery(id+"F17.imprint","IMPRINT",FACE,{"disambiguationData":[TD([[makeQuery(id+"F17.imprint","IMPRINT",EDGE,{"derivedFrom":sQuery(id+"F17.wireOp",EDGE,"E59.8.0.0")}),1.0]])]});
            var Q68;
            Q68=makeQuery(id+"F17.imprint","IMPRINT",FACE,{"disambiguationData":[TD([[makeQuery(id+"F17.imprint","IMPRINT",EDGE,{"derivedFrom":sQuery(id+"F17.wireOp",EDGE,"E59.1.0.0")}),1.0]])]});
            var Q69;
            Q69=makeQuery(id+"F17.imprint","IMPRINT",FACE,{"disambiguationData":[TD([[makeQuery(id+"F17.imprint","IMPRINT",EDGE,{"derivedFrom":sQuery(id+"F17.wireOp",EDGE,"E59.2.6.0")}),1.0]])]});
            var Q70;
            Q70=sQuery(id+"F17.wireOp",EDGE,"E59.5.2.0");
            var Q71;
            Q71=sQuery(id+"F17.wireOp",EDGE,"E59.9.1.0");
            var Q72;
            Q72=sQuery(id+"F17.wireOp",EDGE,"E59.5.6.0");
            var Q73;
            Q73=sQuery(id+"F17.wireOp",EDGE,"E59.8.4.0");
            var Q74;
            Q74=sQuery(id+"F17.wireOp",EDGE,"E59.2.0.0");
            var Q75;
            Q75=sQuery(id+"F17.wireOp",EDGE,"E59.0.4.0");
            var Q76;
            Q76=sQuery(id+"F17.wireOp",EDGE,"E59.8.5.0");
            var Q77;
            Q77=sQuery(id+"F17.wireOp",EDGE,"E59.8.3.0");
            var Q78;
            Q78=sQuery(id+"F17.wireOp",EDGE,"E59.1.3.0");
            var Q79;
            Q79=sQuery(id+"F17.wireOp",EDGE,"E59.3.4.0");
            var Q80;
            Q80=sQuery(id+"F17.wireOp",EDGE,"E59.5.5.0");
            var Q81;
            Q81=sQuery(id+"F17.wireOp",EDGE,"E59.3.1.0");
            var Q82;
            Q82=sQuery(id+"F17.wireOp",EDGE,"E59.7.1.0");
            var Q83;
            Q83=sQuery(id+"F17.wireOp",EDGE,"E59.9.6.0");
            var Q84;
            Q84=sQuery(id+"F17.wireOp",EDGE,"E59.6.2.0");
            var Q85;
            Q85=sQuery(id+"F17.wireOp",EDGE,"E59.9.5.0");
            var Q86;
            Q86=sQuery(id+"F17.wireOp",EDGE,"E59.1.0.0");
            var Q87;
            Q87=sQuery(id+"F17.wireOp",EDGE,"E59.0.1.0");
            var Q88;
            Q88=sQuery(id+"F17.wireOp",EDGE,"E59.2.6.0");
            var Q89;
            Q89=sQuery(id+"F17.wireOp",EDGE,"E59.1.1.0");
            var Q90;
            Q90=sQuery(id+"F17.wireOp",EDGE,"E59.8.0.0");
            var Q91;
            Q91=sQuery(id+"F17.wireOp",EDGE,"E59.7.2.0");
            var Q92;
            Q92=sQuery(id+"F17.wireOp",EDGE,"E59.8.2.0");
            var Q93;
            Q93=sQuery(id+"F17.wireOp",EDGE,"E59.8.6.0");
            var Q94;
            Q94=sQuery(id+"F17.wireOp",EDGE,"E59.4.0.0");
            var Q95;
            Q95=sQuery(id+"F17.wireOp",EDGE,"E59.5.4.0");
            var Q96;
            Q96=sQuery(id+"F17.wireOp",EDGE,"E59.0.5.0");
            var Q97;
            Q97=sQuery(id+"F17.wireOp",EDGE,"E59.0.6.0");
            var Q98;
            Q98=sQuery(id+"F17.wireOp",EDGE,"E59.8.1.0");
            var Q99;
            Q99=sQuery(id+"F17.wireOp",EDGE,"E59.1.5.0");
            var Q100;
            Q100=sQuery(id+"F17.wireOp",EDGE,"E59.1.6.0");
            var Q101;
            Q101=sQuery(id+"F17.wireOp",EDGE,"E59.3.3.0");
            var Q102;
            Q102=sQuery(id+"F17.wireOp",EDGE,"E59.6.3.0");
            var Q103;
            Q103=sQuery(id+"F17.wireOp",EDGE,"E59.2.3.0");
            var Q104;
            Q104=sQuery(id+"F17.wireOp",EDGE,"E59.6.5.0");
            var Q105;
            Q105=sQuery(id+"F17.wireOp",EDGE,"E59.6.6.0");
            var Q106;
            Q106=sQuery(id+"F17.wireOp",EDGE,"E59.4.3.0");
            var Q107;
            Q107=sQuery(id+"F17.wireOp",EDGE,"E59.4.5.0");
            var Q108;
            Q108=sQuery(id+"F17.wireOp",EDGE,"E59.2.1.0");
            var Q109;
            Q109=sQuery(id+"F17.wireOp",EDGE,"E59.4.2.0");
            var Q110;
            Q110=sQuery(id+"F17.wireOp",EDGE,"E59.9.2.0");
            var Q111;
            Q111=sQuery(id+"F17.wireOp",EDGE,"E59.5.3.0");
            var Q112;
            Q112=sQuery(id+"F17.wireOp",EDGE,"E59.9.0.0");
            var Q113;
            Q113=sQuery(id+"F17.wireOp",EDGE,"E59.4.1.0");
            var Q114;
            Q114=sQuery(id+"F17.wireOp",EDGE,"E59.4.6.0");
            var Q115;
            Q115=sQuery(id+"F17.wireOp",EDGE,"E58");
            var Q116;
            Q116=sQuery(id+"F17.wireOp",EDGE,"E59.5.1.0");
            var Q117;
            Q117=sQuery(id+"F17.wireOp",EDGE,"E59.7.0.0");
            var Q118;
            Q118=sQuery(id+"F17.wireOp",EDGE,"E59.7.6.0");
            var Q119;
            Q119=sQuery(id+"F17.wireOp",EDGE,"E59.2.4.0");
            var Q120;
            Q120=sQuery(id+"F17.wireOp",EDGE,"E59.0.3.0");
            var Q121;
            Q121=sQuery(id+"F17.wireOp",EDGE,"E59.7.3.0");
            var Q122;
            Q122=sQuery(id+"F17.wireOp",EDGE,"E59.1.4.0");
            var Q123;
            Q123=sQuery(id+"F17.wireOp",EDGE,"E59.1.2.0");
            var Q124;
            Q124=sQuery(id+"F17.wireOp",EDGE,"E59.6.4.0");
            var Q125;
            Q125=sQuery(id+"F17.wireOp",EDGE,"E59.5.0.0");
            var Q126;
            Q126=sQuery(id+"F17.wireOp",EDGE,"E59.7.4.0");
            var Q127;
            Q127=sQuery(id+"F17.wireOp",EDGE,"E59.2.5.0");
            var Q128;
            Q128=sQuery(id+"F17.wireOp",EDGE,"E59.0.2.0");
            var Q129;
            Q129=sQuery(id+"F17.wireOp",EDGE,"E59.9.3.0");
            var Q130;
            Q130=sQuery(id+"F17.wireOp",EDGE,"E59.3.2.0");
            var Q131;
            Q131=sQuery(id+"F17.wireOp",EDGE,"E59.9.4.0");
            var Q132;
            Q132=sQuery(id+"F17.wireOp",EDGE,"E59.3.6.0");
            var Q133;
            Q133=sQuery(id+"F17.wireOp",EDGE,"E59.3.5.0");
            var Q134;
            Q134=sQuery(id+"F17.wireOp",EDGE,"E59.3.0.0");
            var Q135;
            Q135=sQuery(id+"F17.wireOp",EDGE,"E59.4.4.0");
            var Q136;
            Q136=sQuery(id+"F17.wireOp",EDGE,"E59.2.2.0");
            var Q137;
            Q137=sQuery(id+"F17.wireOp",EDGE,"E59.6.1.0");
            var Q138;
            Q138=sQuery(id+"F17.wireOp",EDGE,"E59.7.5.0");
            var Q139;
            Q139=sQuery(id+"F17.wireOp",EDGE,"E59.6.0.0");
            extrude(context, id + "F18", {"entities" : qUnion([Q0, Q1, Q2, Q3, Q4, Q5, Q6, Q7, Q8, Q9, Q10, Q11, Q12, Q13, Q14, Q15, Q16, Q17, Q18, Q19, Q20, Q21, Q22, Q23, Q24, Q25, Q26, Q27, Q28, Q29, Q30, Q31, Q32, Q33, Q34, Q35, Q36, Q37, Q38, Q39, Q40, Q41, Q42, Q43, Q44, Q45, Q46, Q47, Q48, Q49, Q50, Q51, Q52, Q53, Q54, Q55, Q56, Q57, Q58, Q59, Q60, Q61, Q62, Q63, Q64, Q65, Q66, Q67, Q68, Q69]), "operationType" : NewBodyOperationType.REMOVE, "surfaceEntities" : qUnion([Q70, Q71, Q72, Q73, Q74, Q75, Q76, Q77, Q78, Q79, Q80, Q81, Q82, Q83, Q84, Q85, Q86, Q87, Q88, Q89, Q90, Q91, Q92, Q93, Q94, Q95, Q96, Q97, Q98, Q99, Q100, Q101, Q102, Q103, Q104, Q105, Q106, Q107, Q108, Q109, Q110, Q111, Q112, Q113, Q114, Q115, Q116, Q117, Q118, Q119, Q120, Q121, Q122, Q123, Q124, Q125, Q126, Q127, Q128, Q129, Q130, Q131, Q132, Q133, Q134, Q135, Q136, Q137, Q138, Q139]), "endBound" : BoundingType.UP_TO_NEXT, "oppositeDirection" : true, "depth" : 25 * mm, "offsetDistance" : 25 * mm});
        }
        {
            var Q0;
            Q0=makeQuery(id+"F2.opExtrude","SWEPT_FACE",FACE,{"disambiguationData":[OSD([sQuery(id+"F0.wireOp",EDGE,"E1.top")])]});
            var sketch = newSketch(context, id + "F19", { "sketchPlane" : qUnion([Q0])});
            skCircle(sketch, "E60", {"center": v(-58.73, 80) * mm, "radius": 2.5 * mm});
            skCircle(sketch, "E61.0.1.0", {"center": v(-58.73, 67.5) * mm, "radius": 2.5 * mm});
            skCircle(sketch, "E61.0.2.0", {"center": v(-58.73, 55) * mm, "radius": 2.5 * mm});
            skCircle(sketch, "E61.0.3.0", {"center": v(-58.73, 42.5) * mm, "radius": 2.5 * mm});
            skCircle(sketch, "E61.0.4.0", {"center": v(-58.73, 30) * mm, "radius": 2.5 * mm});
            skCircle(sketch, "E61.0.5.0", {"center": v(-58.73, 17.5) * mm, "radius": 2.5 * mm});
            skCircle(sketch, "E61.1.0.0", {"center": v(-46.23, 80) * mm, "radius": 2.5 * mm});
            skCircle(sketch, "E61.1.1.0", {"center": v(-46.23, 67.5) * mm, "radius": 2.5 * mm});
            skCircle(sketch, "E61.1.2.0", {"center": v(-46.23, 55) * mm, "radius": 2.5 * mm});
            skCircle(sketch, "E61.1.3.0", {"center": v(-46.23, 42.5) * mm, "radius": 2.5 * mm});
            skCircle(sketch, "E61.1.4.0", {"center": v(-46.23, 30) * mm, "radius": 2.5 * mm});
            skCircle(sketch, "E61.1.5.0", {"center": v(-46.23, 17.5) * mm, "radius": 2.5 * mm});
            skCircle(sketch, "E61.2.0.0", {"center": v(-33.73, 80) * mm, "radius": 2.5 * mm});
            skCircle(sketch, "E61.2.1.0", {"center": v(-33.73, 67.5) * mm, "radius": 2.5 * mm});
            skCircle(sketch, "E61.2.2.0", {"center": v(-33.73, 55) * mm, "radius": 2.5 * mm});
            skCircle(sketch, "E61.2.3.0", {"center": v(-33.73, 42.5) * mm, "radius": 2.5 * mm});
            skCircle(sketch, "E61.2.4.0", {"center": v(-33.73, 30) * mm, "radius": 2.5 * mm});
            skCircle(sketch, "E61.2.5.0", {"center": v(-33.73, 17.5) * mm, "radius": 2.5 * mm});
            skCircle(sketch, "E61.3.0.0", {"center": v(-21.23, 80) * mm, "radius": 2.5 * mm});
            skCircle(sketch, "E61.3.1.0", {"center": v(-21.23, 67.5) * mm, "radius": 2.5 * mm});
            skCircle(sketch, "E61.3.2.0", {"center": v(-21.23, 55) * mm, "radius": 2.5 * mm});
            skCircle(sketch, "E61.3.3.0", {"center": v(-21.23, 42.5) * mm, "radius": 2.5 * mm});
            skCircle(sketch, "E61.3.4.0", {"center": v(-21.23, 30) * mm, "radius": 2.5 * mm});
            skCircle(sketch, "E61.3.5.0", {"center": v(-21.23, 17.5) * mm, "radius": 2.5 * mm});
            skCircle(sketch, "E61.4.0.0", {"center": v(-8.73, 80) * mm, "radius": 2.5 * mm});
            skCircle(sketch, "E61.4.1.0", {"center": v(-8.73, 67.5) * mm, "radius": 2.5 * mm});
            skCircle(sketch, "E61.4.2.0", {"center": v(-8.73, 55) * mm, "radius": 2.5 * mm});
            skCircle(sketch, "E61.4.3.0", {"center": v(-8.73, 42.5) * mm, "radius": 2.5 * mm});
            skCircle(sketch, "E61.4.4.0", {"center": v(-8.73, 30) * mm, "radius": 2.5 * mm});
            skCircle(sketch, "E61.4.5.0", {"center": v(-8.73, 17.5) * mm, "radius": 2.5 * mm});
            skCircle(sketch, "E61.5.0.0", {"center": v(3.77, 80) * mm, "radius": 2.5 * mm});
            skCircle(sketch, "E61.5.1.0", {"center": v(3.77, 67.5) * mm, "radius": 2.5 * mm});
            skCircle(sketch, "E61.5.2.0", {"center": v(3.77, 55) * mm, "radius": 2.5 * mm});
            skCircle(sketch, "E61.5.3.0", {"center": v(3.77, 42.5) * mm, "radius": 2.5 * mm});
            skCircle(sketch, "E61.5.4.0", {"center": v(3.77, 30) * mm, "radius": 2.5 * mm});
            skCircle(sketch, "E61.5.5.0", {"center": v(3.77, 17.5) * mm, "radius": 2.5 * mm});
            skCircle(sketch, "E61.6.0.0", {"center": v(16.27, 80) * mm, "radius": 2.5 * mm});
            skCircle(sketch, "E61.6.1.0", {"center": v(16.27, 67.5) * mm, "radius": 2.5 * mm});
            skCircle(sketch, "E61.6.2.0", {"center": v(16.27, 55) * mm, "radius": 2.5 * mm});
            skCircle(sketch, "E61.6.3.0", {"center": v(16.27, 42.5) * mm, "radius": 2.5 * mm});
            skCircle(sketch, "E61.6.4.0", {"center": v(16.27, 30) * mm, "radius": 2.5 * mm});
            skCircle(sketch, "E61.6.5.0", {"center": v(16.27, 17.5) * mm, "radius": 2.5 * mm});
            skCircle(sketch, "E61.7.0.0", {"center": v(28.77, 80) * mm, "radius": 2.5 * mm});
            skCircle(sketch, "E61.7.1.0", {"center": v(28.77, 67.5) * mm, "radius": 2.5 * mm});
            skCircle(sketch, "E61.7.2.0", {"center": v(28.77, 55) * mm, "radius": 2.5 * mm});
            skCircle(sketch, "E61.7.3.0", {"center": v(28.77, 42.5) * mm, "radius": 2.5 * mm});
            skCircle(sketch, "E61.7.4.0", {"center": v(28.77, 30) * mm, "radius": 2.5 * mm});
            skCircle(sketch, "E61.7.5.0", {"center": v(28.77, 17.5) * mm, "radius": 2.5 * mm});
            skCircle(sketch, "E61.8.0.0", {"center": v(41.27, 80) * mm, "radius": 2.5 * mm});
            skCircle(sketch, "E61.8.1.0", {"center": v(41.27, 67.5) * mm, "radius": 2.5 * mm});
            skCircle(sketch, "E61.8.2.0", {"center": v(41.27, 55) * mm, "radius": 2.5 * mm});
            skCircle(sketch, "E61.8.3.0", {"center": v(41.27, 42.5) * mm, "radius": 2.5 * mm});
            skCircle(sketch, "E61.8.4.0", {"center": v(41.27, 30) * mm, "radius": 2.5 * mm});
            skCircle(sketch, "E61.8.5.0", {"center": v(41.27, 17.5) * mm, "radius": 2.5 * mm});
            skCircle(sketch, "E61.9.0.0", {"center": v(53.77, 80) * mm, "radius": 2.5 * mm});
            skCircle(sketch, "E61.9.1.0", {"center": v(53.77, 67.5) * mm, "radius": 2.5 * mm});
            skCircle(sketch, "E61.9.2.0", {"center": v(53.77, 55) * mm, "radius": 2.5 * mm});
            skCircle(sketch, "E61.9.3.0", {"center": v(53.77, 42.5) * mm, "radius": 2.5 * mm});
            skCircle(sketch, "E61.9.4.0", {"center": v(53.77, 30) * mm, "radius": 2.5 * mm});
            skCircle(sketch, "E61.9.5.0", {"center": v(53.77, 17.5) * mm, "radius": 2.5 * mm});
            skLineSegment(sketch, "E61.direction1", {"start": v(-58.73, 80) * mm, "end": v(-46.23, 80) * mm, "construction": true});
            skLineSegment(sketch, "E61.direction2", {"start": v(-58.73, 80) * mm, "end": v(-58.73, 67.5) * mm, "construction": true});
            skSolve(sketch);
        }
        {
            var Q0;
            Q0=makeQuery(id+"F19.imprint","IMPRINT",FACE,{"disambiguationData":[TD([[makeQuery(id+"F19.imprint","IMPRINT",EDGE,{"derivedFrom":sQuery(id+"F19.wireOp",EDGE,"E61.7.2.0")}),1.0]])]});
            var Q1;
            Q1=makeQuery(id+"F19.imprint","IMPRINT",FACE,{"disambiguationData":[TD([[makeQuery(id+"F19.imprint","IMPRINT",EDGE,{"derivedFrom":sQuery(id+"F19.wireOp",EDGE,"E61.7.0.0")}),1.0]])]});
            var Q2;
            Q2=makeQuery(id+"F19.imprint","IMPRINT",FACE,{"disambiguationData":[TD([[makeQuery(id+"F19.imprint","IMPRINT",EDGE,{"derivedFrom":sQuery(id+"F19.wireOp",EDGE,"E61.0.4.0")}),1.0]])]});
            var Q3;
            Q3=makeQuery(id+"F19.imprint","IMPRINT",FACE,{"disambiguationData":[TD([[makeQuery(id+"F19.imprint","IMPRINT",EDGE,{"derivedFrom":sQuery(id+"F19.wireOp",EDGE,"E61.5.2.0")}),1.0]])]});
            var Q4;
            Q4=makeQuery(id+"F19.imprint","IMPRINT",FACE,{"disambiguationData":[TD([[makeQuery(id+"F19.imprint","IMPRINT",EDGE,{"derivedFrom":sQuery(id+"F19.wireOp",EDGE,"E61.5.1.0")}),1.0]])]});
            var Q5;
            Q5=makeQuery(id+"F19.imprint","IMPRINT",FACE,{"disambiguationData":[TD([[makeQuery(id+"F19.imprint","IMPRINT",EDGE,{"derivedFrom":sQuery(id+"F19.wireOp",EDGE,"E61.0.5.0")}),1.0]])]});
            var Q6;
            Q6=makeQuery(id+"F19.imprint","IMPRINT",FACE,{"disambiguationData":[TD([[makeQuery(id+"F19.imprint","IMPRINT",EDGE,{"derivedFrom":sQuery(id+"F19.wireOp",EDGE,"E61.9.0.0")}),1.0]])]});
            var Q7;
            Q7=makeQuery(id+"F19.imprint","IMPRINT",FACE,{"disambiguationData":[TD([[makeQuery(id+"F19.imprint","IMPRINT",EDGE,{"derivedFrom":sQuery(id+"F19.wireOp",EDGE,"E61.3.1.0")}),1.0]])]});
            var Q8;
            Q8=makeQuery(id+"F19.imprint","IMPRINT",FACE,{"disambiguationData":[TD([[makeQuery(id+"F19.imprint","IMPRINT",EDGE,{"derivedFrom":sQuery(id+"F19.wireOp",EDGE,"E61.1.3.0")}),1.0]])]});
            var Q9;
            Q9=makeQuery(id+"F19.imprint","IMPRINT",FACE,{"disambiguationData":[TD([[makeQuery(id+"F19.imprint","IMPRINT",EDGE,{"derivedFrom":sQuery(id+"F19.wireOp",EDGE,"E61.9.5.0")}),1.0]])]});
            var Q10;
            Q10=makeQuery(id+"F19.imprint","IMPRINT",FACE,{"disambiguationData":[TD([[makeQuery(id+"F19.imprint","IMPRINT",EDGE,{"derivedFrom":sQuery(id+"F19.wireOp",EDGE,"E61.4.1.0")}),1.0]])]});
            var Q11;
            Q11=makeQuery(id+"F19.imprint","IMPRINT",FACE,{"disambiguationData":[TD([[makeQuery(id+"F19.imprint","IMPRINT",EDGE,{"derivedFrom":sQuery(id+"F19.wireOp",EDGE,"E61.2.3.0")}),1.0]])]});
            var Q12;
            Q12=makeQuery(id+"F19.imprint","IMPRINT",FACE,{"disambiguationData":[TD([[makeQuery(id+"F19.imprint","IMPRINT",EDGE,{"derivedFrom":sQuery(id+"F19.wireOp",EDGE,"E61.4.5.0")}),1.0]])]});
            var Q13;
            Q13=makeQuery(id+"F19.imprint","IMPRINT",FACE,{"disambiguationData":[TD([[makeQuery(id+"F19.imprint","IMPRINT",EDGE,{"derivedFrom":sQuery(id+"F19.wireOp",EDGE,"E61.5.0.0")}),1.0]])]});
            var Q14;
            Q14=makeQuery(id+"F19.imprint","IMPRINT",FACE,{"disambiguationData":[TD([[makeQuery(id+"F19.imprint","IMPRINT",EDGE,{"derivedFrom":sQuery(id+"F19.wireOp",EDGE,"E61.2.4.0")}),1.0]])]});
            var Q15;
            Q15=makeQuery(id+"F19.imprint","IMPRINT",FACE,{"disambiguationData":[TD([[makeQuery(id+"F19.imprint","IMPRINT",EDGE,{"derivedFrom":sQuery(id+"F19.wireOp",EDGE,"E61.0.2.0")}),1.0]])]});
            var Q16;
            Q16=makeQuery(id+"F19.imprint","IMPRINT",FACE,{"disambiguationData":[TD([[makeQuery(id+"F19.imprint","IMPRINT",EDGE,{"derivedFrom":sQuery(id+"F19.wireOp",EDGE,"E61.9.4.0")}),1.0]])]});
            var Q17;
            Q17=makeQuery(id+"F19.imprint","IMPRINT",FACE,{"disambiguationData":[TD([[makeQuery(id+"F19.imprint","IMPRINT",EDGE,{"derivedFrom":sQuery(id+"F19.wireOp",EDGE,"E61.8.4.0")}),1.0]])]});
            var Q18;
            Q18=makeQuery(id+"F19.imprint","IMPRINT",FACE,{"disambiguationData":[TD([[makeQuery(id+"F19.imprint","IMPRINT",EDGE,{"derivedFrom":sQuery(id+"F19.wireOp",EDGE,"E61.7.4.0")}),1.0]])]});
            var Q19;
            Q19=makeQuery(id+"F19.imprint","IMPRINT",FACE,{"disambiguationData":[TD([[makeQuery(id+"F19.imprint","IMPRINT",EDGE,{"derivedFrom":sQuery(id+"F19.wireOp",EDGE,"E61.1.0.0")}),1.0]])]});
            var Q20;
            Q20=makeQuery(id+"F19.imprint","IMPRINT",FACE,{"disambiguationData":[TD([[makeQuery(id+"F19.imprint","IMPRINT",EDGE,{"derivedFrom":sQuery(id+"F19.wireOp",EDGE,"E61.8.3.0")}),1.0]])]});
            var Q21;
            Q21=makeQuery(id+"F19.imprint","IMPRINT",FACE,{"disambiguationData":[TD([[makeQuery(id+"F19.imprint","IMPRINT",EDGE,{"derivedFrom":sQuery(id+"F19.wireOp",EDGE,"E61.6.1.0")}),1.0]])]});
            var Q22;
            Q22=makeQuery(id+"F19.imprint","IMPRINT",FACE,{"disambiguationData":[TD([[makeQuery(id+"F19.imprint","IMPRINT",EDGE,{"derivedFrom":sQuery(id+"F19.wireOp",EDGE,"E61.6.2.0")}),1.0]])]});
            var Q23;
            Q23=makeQuery(id+"F19.imprint","IMPRINT",FACE,{"disambiguationData":[TD([[makeQuery(id+"F19.imprint","IMPRINT",EDGE,{"derivedFrom":sQuery(id+"F19.wireOp",EDGE,"E61.4.0.0")}),1.0]])]});
            var Q24;
            Q24=makeQuery(id+"F19.imprint","IMPRINT",FACE,{"disambiguationData":[TD([[makeQuery(id+"F19.imprint","IMPRINT",EDGE,{"derivedFrom":sQuery(id+"F19.wireOp",EDGE,"E61.8.5.0")}),1.0]])]});
            var Q25;
            Q25=makeQuery(id+"F19.imprint","IMPRINT",FACE,{"disambiguationData":[TD([[makeQuery(id+"F19.imprint","IMPRINT",EDGE,{"derivedFrom":sQuery(id+"F19.wireOp",EDGE,"E61.7.3.0")}),1.0]])]});
            var Q26;
            Q26=makeQuery(id+"F19.imprint","IMPRINT",FACE,{"disambiguationData":[TD([[makeQuery(id+"F19.imprint","IMPRINT",EDGE,{"derivedFrom":sQuery(id+"F19.wireOp",EDGE,"E61.3.0.0")}),1.0]])]});
            var Q27;
            Q27=makeQuery(id+"F19.imprint","IMPRINT",FACE,{"disambiguationData":[TD([[makeQuery(id+"F19.imprint","IMPRINT",EDGE,{"derivedFrom":sQuery(id+"F19.wireOp",EDGE,"E61.1.2.0")}),1.0]])]});
            var Q28;
            Q28=makeQuery(id+"F19.imprint","IMPRINT",FACE,{"disambiguationData":[TD([[makeQuery(id+"F19.imprint","IMPRINT",EDGE,{"derivedFrom":sQuery(id+"F19.wireOp",EDGE,"E61.8.0.0")}),1.0]])]});
            var Q29;
            Q29=makeQuery(id+"F19.imprint","IMPRINT",FACE,{"disambiguationData":[TD([[makeQuery(id+"F19.imprint","IMPRINT",EDGE,{"derivedFrom":sQuery(id+"F19.wireOp",EDGE,"E61.9.1.0")}),1.0]])]});
            var Q30;
            Q30=makeQuery(id+"F19.imprint","IMPRINT",FACE,{"disambiguationData":[TD([[makeQuery(id+"F19.imprint","IMPRINT",EDGE,{"derivedFrom":sQuery(id+"F19.wireOp",EDGE,"E61.1.1.0")}),1.0]])]});
            var Q31;
            Q31=makeQuery(id+"F19.imprint","IMPRINT",FACE,{"disambiguationData":[TD([[makeQuery(id+"F19.imprint","IMPRINT",EDGE,{"derivedFrom":sQuery(id+"F19.wireOp",EDGE,"E61.4.4.0")}),1.0]])]});
            var Q32;
            Q32=makeQuery(id+"F19.imprint","IMPRINT",FACE,{"disambiguationData":[TD([[makeQuery(id+"F19.imprint","IMPRINT",EDGE,{"derivedFrom":sQuery(id+"F19.wireOp",EDGE,"E61.5.4.0")}),1.0]])]});
            var Q33;
            Q33=makeQuery(id+"F19.imprint","IMPRINT",FACE,{"disambiguationData":[TD([[makeQuery(id+"F19.imprint","IMPRINT",EDGE,{"derivedFrom":sQuery(id+"F19.wireOp",EDGE,"E61.4.3.0")}),1.0]])]});
            var Q34;
            Q34=makeQuery(id+"F19.imprint","IMPRINT",FACE,{"disambiguationData":[TD([[makeQuery(id+"F19.imprint","IMPRINT",EDGE,{"derivedFrom":sQuery(id+"F19.wireOp",EDGE,"E61.6.4.0")}),1.0]])]});
            var Q35;
            Q35=makeQuery(id+"F19.imprint","IMPRINT",FACE,{"disambiguationData":[TD([[makeQuery(id+"F19.imprint","IMPRINT",EDGE,{"derivedFrom":sQuery(id+"F19.wireOp",EDGE,"E61.6.3.0")}),1.0]])]});
            var Q36;
            Q36=makeQuery(id+"F19.imprint","IMPRINT",FACE,{"disambiguationData":[TD([[makeQuery(id+"F19.imprint","IMPRINT",EDGE,{"derivedFrom":sQuery(id+"F19.wireOp",EDGE,"E61.2.1.0")}),1.0]])]});
            var Q37;
            Q37=makeQuery(id+"F19.imprint","IMPRINT",FACE,{"disambiguationData":[TD([[makeQuery(id+"F19.imprint","IMPRINT",EDGE,{"derivedFrom":sQuery(id+"F19.wireOp",EDGE,"E61.6.5.0")}),1.0]])]});
            var Q38;
            Q38=makeQuery(id+"F19.imprint","IMPRINT",FACE,{"disambiguationData":[TD([[makeQuery(id+"F19.imprint","IMPRINT",EDGE,{"derivedFrom":sQuery(id+"F19.wireOp",EDGE,"E61.8.2.0")}),1.0]])]});
            var Q39;
            Q39=makeQuery(id+"F19.imprint","IMPRINT",FACE,{"disambiguationData":[TD([[makeQuery(id+"F19.imprint","IMPRINT",EDGE,{"derivedFrom":sQuery(id+"F19.wireOp",EDGE,"E61.9.3.0")}),1.0]])]});
            var Q40;
            Q40=makeQuery(id+"F19.imprint","IMPRINT",FACE,{"disambiguationData":[TD([[makeQuery(id+"F19.imprint","IMPRINT",EDGE,{"derivedFrom":sQuery(id+"F19.wireOp",EDGE,"E61.5.5.0")}),1.0]])]});
            var Q41;
            Q41=makeQuery(id+"F19.imprint","IMPRINT",FACE,{"disambiguationData":[TD([[makeQuery(id+"F19.imprint","IMPRINT",EDGE,{"derivedFrom":sQuery(id+"F19.wireOp",EDGE,"E61.0.1.0")}),1.0]])]});
            var Q42;
            Q42=makeQuery(id+"F19.imprint","IMPRINT",FACE,{"disambiguationData":[TD([[makeQuery(id+"F19.imprint","IMPRINT",EDGE,{"derivedFrom":sQuery(id+"F19.wireOp",EDGE,"E61.7.1.0")}),1.0]])]});
            var Q43;
            Q43=makeQuery(id+"F19.imprint","IMPRINT",FACE,{"disambiguationData":[TD([[makeQuery(id+"F19.imprint","IMPRINT",EDGE,{"derivedFrom":sQuery(id+"F19.wireOp",EDGE,"E61.7.5.0")}),1.0]])]});
            var Q44;
            Q44=makeQuery(id+"F19.imprint","IMPRINT",FACE,{"disambiguationData":[TD([[makeQuery(id+"F19.imprint","IMPRINT",EDGE,{"derivedFrom":sQuery(id+"F19.wireOp",EDGE,"E61.0.3.0")}),1.0]])]});
            var Q45;
            Q45=makeQuery(id+"F19.imprint","IMPRINT",FACE,{"disambiguationData":[TD([[makeQuery(id+"F19.imprint","IMPRINT",EDGE,{"derivedFrom":sQuery(id+"F19.wireOp",EDGE,"E60")}),1.0]])]});
            var Q46;
            Q46=makeQuery(id+"F19.imprint","IMPRINT",FACE,{"disambiguationData":[TD([[makeQuery(id+"F19.imprint","IMPRINT",EDGE,{"derivedFrom":sQuery(id+"F19.wireOp",EDGE,"E61.6.0.0")}),1.0]])]});
            var Q47;
            Q47=makeQuery(id+"F19.imprint","IMPRINT",FACE,{"disambiguationData":[TD([[makeQuery(id+"F19.imprint","IMPRINT",EDGE,{"derivedFrom":sQuery(id+"F19.wireOp",EDGE,"E61.5.3.0")}),1.0]])]});
            var Q48;
            Q48=makeQuery(id+"F19.imprint","IMPRINT",FACE,{"disambiguationData":[TD([[makeQuery(id+"F19.imprint","IMPRINT",EDGE,{"derivedFrom":sQuery(id+"F19.wireOp",EDGE,"E61.3.2.0")}),1.0]])]});
            var Q49;
            Q49=makeQuery(id+"F19.imprint","IMPRINT",FACE,{"disambiguationData":[TD([[makeQuery(id+"F19.imprint","IMPRINT",EDGE,{"derivedFrom":sQuery(id+"F19.wireOp",EDGE,"E61.8.1.0")}),1.0]])]});
            var Q50;
            Q50=makeQuery(id+"F19.imprint","IMPRINT",FACE,{"disambiguationData":[TD([[makeQuery(id+"F19.imprint","IMPRINT",EDGE,{"derivedFrom":sQuery(id+"F19.wireOp",EDGE,"E61.3.5.0")}),1.0]])]});
            var Q51;
            Q51=makeQuery(id+"F19.imprint","IMPRINT",FACE,{"disambiguationData":[TD([[makeQuery(id+"F19.imprint","IMPRINT",EDGE,{"derivedFrom":sQuery(id+"F19.wireOp",EDGE,"E61.9.2.0")}),1.0]])]});
            var Q52;
            Q52=makeQuery(id+"F19.imprint","IMPRINT",FACE,{"disambiguationData":[TD([[makeQuery(id+"F19.imprint","IMPRINT",EDGE,{"derivedFrom":sQuery(id+"F19.wireOp",EDGE,"E61.2.5.0")}),1.0]])]});
            var Q53;
            Q53=makeQuery(id+"F19.imprint","IMPRINT",FACE,{"disambiguationData":[TD([[makeQuery(id+"F19.imprint","IMPRINT",EDGE,{"derivedFrom":sQuery(id+"F19.wireOp",EDGE,"E61.3.4.0")}),1.0]])]});
            var Q54;
            Q54=makeQuery(id+"F19.imprint","IMPRINT",FACE,{"disambiguationData":[TD([[makeQuery(id+"F19.imprint","IMPRINT",EDGE,{"derivedFrom":sQuery(id+"F19.wireOp",EDGE,"E61.1.5.0")}),1.0]])]});
            var Q55;
            Q55=makeQuery(id+"F19.imprint","IMPRINT",FACE,{"disambiguationData":[TD([[makeQuery(id+"F19.imprint","IMPRINT",EDGE,{"derivedFrom":sQuery(id+"F19.wireOp",EDGE,"E61.2.2.0")}),1.0]])]});
            var Q56;
            Q56=makeQuery(id+"F19.imprint","IMPRINT",FACE,{"disambiguationData":[TD([[makeQuery(id+"F19.imprint","IMPRINT",EDGE,{"derivedFrom":sQuery(id+"F19.wireOp",EDGE,"E61.3.3.0")}),1.0]])]});
            var Q57;
            Q57=makeQuery(id+"F19.imprint","IMPRINT",FACE,{"disambiguationData":[TD([[makeQuery(id+"F19.imprint","IMPRINT",EDGE,{"derivedFrom":sQuery(id+"F19.wireOp",EDGE,"E61.1.4.0")}),1.0]])]});
            var Q58;
            Q58=makeQuery(id+"F19.imprint","IMPRINT",FACE,{"disambiguationData":[TD([[makeQuery(id+"F19.imprint","IMPRINT",EDGE,{"derivedFrom":sQuery(id+"F19.wireOp",EDGE,"E61.2.0.0")}),1.0]])]});
            var Q59;
            Q59=makeQuery(id+"F19.imprint","IMPRINT",FACE,{"disambiguationData":[TD([[makeQuery(id+"F19.imprint","IMPRINT",EDGE,{"derivedFrom":sQuery(id+"F19.wireOp",EDGE,"E61.4.2.0")}),1.0]])]});
            extrude(context, id + "F20", {"entities" : qUnion([Q0, Q1, Q2, Q3, Q4, Q5, Q6, Q7, Q8, Q9, Q10, Q11, Q12, Q13, Q14, Q15, Q16, Q17, Q18, Q19, Q20, Q21, Q22, Q23, Q24, Q25, Q26, Q27, Q28, Q29, Q30, Q31, Q32, Q33, Q34, Q35, Q36, Q37, Q38, Q39, Q40, Q41, Q42, Q43, Q44, Q45, Q46, Q47, Q48, Q49, Q50, Q51, Q52, Q53, Q54, Q55, Q56, Q57, Q58, Q59]), "operationType" : NewBodyOperationType.REMOVE, "endBound" : BoundingType.UP_TO_NEXT, "oppositeDirection" : true, "depth" : 25 * mm, "offsetDistance" : 25 * mm});
        }
        {
            var Q0;
            {var subQ0=sQuery(id+"F0.wireOp",EDGE,"E0.right");var subQ1=sQuery(id+"F0.wireOp",EDGE,"E0.bottom");var subQ2=sQuery(id+"F0.wireOp",EDGE,"E0.left");var subQ3=sQuery(id+"F0.wireOp",EDGE,"E0.top");Q0=makeQuery(id+"F16.boolean.opBoolean","MERGE",FACE,{"derivedFrom":[makeQuery(id+"F2.opExtrude","CAP_FACE",FACE,{"disambiguationData":[OSD([subQ1,subQ3,subQ2,subQ0,sQuery(id+"F0.wireOp",EDGE,"E1.bottom"),sQuery(id+"F0.wireOp",EDGE,"E1.top"),sQuery(id+"F0.wireOp",EDGE,"E1.left"),sQuery(id+"F0.wireOp",EDGE,"E1.right")])],"isStart":false}),makeQuery(id+"F16.opExtrude","CAP_FACE",FACE,{"disambiguationData":[OSD([subQ3,subQ0,sQuery(id+"F15.wireOp",EDGE,"E54")])],"isStart":true}),makeQuery(id+"F16.opExtrude","CAP_FACE",FACE,{"disambiguationData":[OSD([subQ3,subQ2,sQuery(id+"F15.wireOp",EDGE,"E55")])],"isStart":true}),makeQuery(id+"F16.opExtrude","CAP_FACE",FACE,{"disambiguationData":[OSD([subQ1,subQ2,sQuery(id+"F15.wireOp",EDGE,"E56")])],"isStart":true}),makeQuery(id+"F16.opExtrude","CAP_FACE",FACE,{"disambiguationData":[OSD([subQ1,subQ0,sQuery(id+"F15.wireOp",EDGE,"E57")])],"isStart":true})]});}
            var sketch = newSketch(context, id + "F21", { "sketchPlane" : qUnion([Q0])});
            skCircle(sketch, "E62", {"center": v(69.5, 99.5) * mm, "radius": 2.65 * mm});
            skCircle(sketch, "E63", {"center": v(69.5, -99.5) * mm, "radius": 2.65 * mm});
            skCircle(sketch, "E64", {"center": v(-69.5, -99.5) * mm, "radius": 2.65 * mm});
            skCircle(sketch, "E65", {"center": v(-69.5, 99.5) * mm, "radius": 2.65 * mm});
            skSolve(sketch);
        }
        {
            var Q0;
            Q0=makeQuery(id+"F21.imprint","IMPRINT",FACE,{"disambiguationData":[TD([[makeQuery(id+"F21.imprint","IMPRINT",EDGE,{"derivedFrom":sQuery(id+"F21.wireOp",EDGE,"E63")}),1.0]])]});
            var Q1;
            Q1=makeQuery(id+"F21.imprint","IMPRINT",FACE,{"disambiguationData":[TD([[makeQuery(id+"F21.imprint","IMPRINT",EDGE,{"derivedFrom":sQuery(id+"F21.wireOp",EDGE,"E64")}),1.0]])]});
            var Q2;
            Q2=makeQuery(id+"F21.imprint","IMPRINT",FACE,{"disambiguationData":[TD([[makeQuery(id+"F21.imprint","IMPRINT",EDGE,{"derivedFrom":sQuery(id+"F21.wireOp",EDGE,"E65")}),1.0]])]});
            var Q3;
            Q3=makeQuery(id+"F21.imprint","IMPRINT",FACE,{"disambiguationData":[TD([[makeQuery(id+"F21.imprint","IMPRINT",EDGE,{"derivedFrom":sQuery(id+"F21.wireOp",EDGE,"E62")}),1.0]])]});
            extrude(context, id + "F22", {"entities" : qUnion([Q0, Q1, Q2, Q3]), "operationType" : NewBodyOperationType.REMOVE, "oppositeDirection" : true, "depth" : 6.2 * mm, "offsetDistance" : 25 * mm});
        }
    });